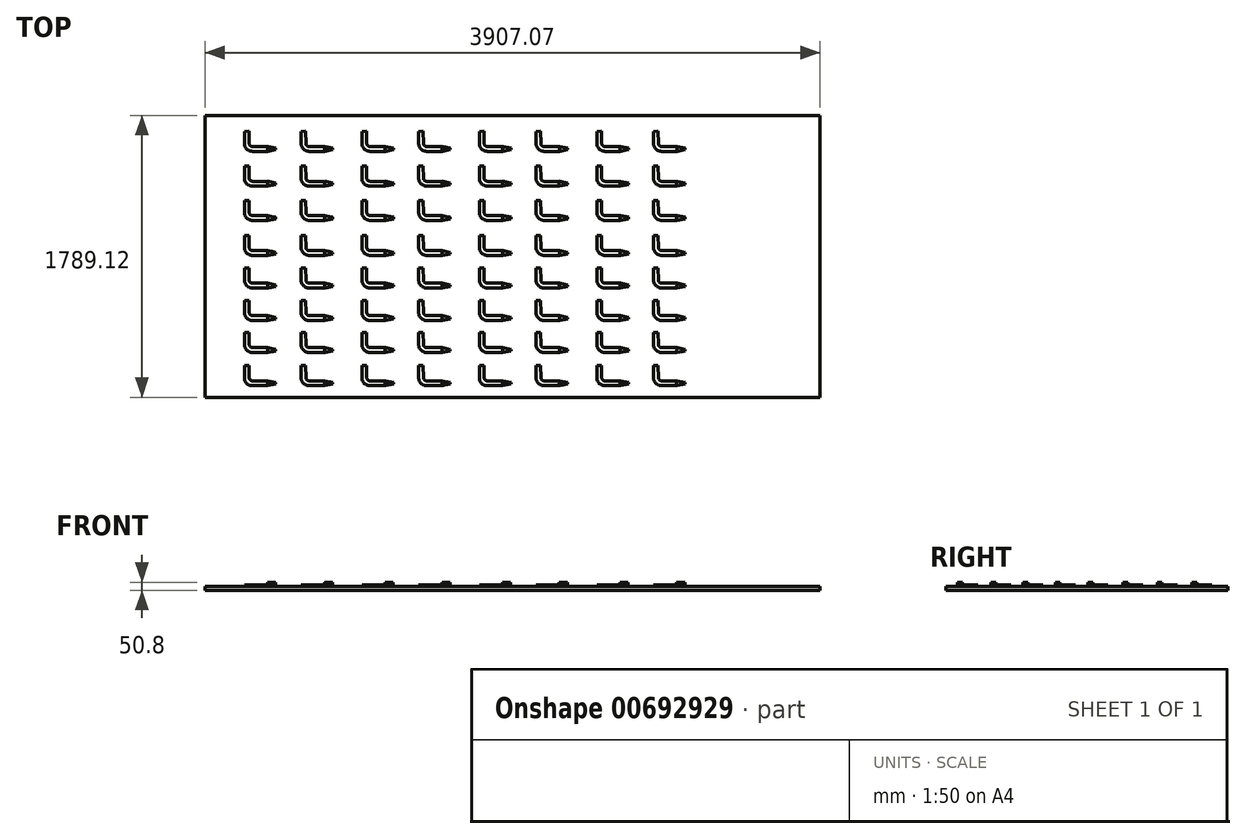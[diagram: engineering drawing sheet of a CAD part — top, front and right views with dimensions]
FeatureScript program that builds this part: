
annotation { "Feature Type Name" : "Feature", "Feature Type Description" : "" }
export const myFeature = defineFeature(function(context is Context, id is Id, definition is map)
    precondition{}
    {
        {
            var Q0;
            Q0=qCreatedBy(makeId("Top.planeOp"),FACE);
            var sketch = newSketch(context, id + "F0", { "sketchPlane" : qUnion([Q0])});
            skLineSegment(sketch, "E0.left", {"start": v(-450.35, 1286.27) * mm, "end": v(-450.35, -502.85) * mm});
            skPoint(sketch, "E0.middle", {"position": v(0, 0) * mm});
            skLineSegment(sketch, "E1", {"start": v(-450.35, 1286.27) * mm, "end": v(3456.72, 1286.27) * mm});
            skLineSegment(sketch, "E2", {"start": v(3456.72, 1286.27) * mm, "end": v(3456.72, -502.85) * mm});
            skLineSegment(sketch, "E3", {"start": v(3456.72, -502.85) * mm, "end": v(-450.35, -502.85) * mm});
            skSolve(sketch);
        }
        {
            var Q0;
            Q0=qSketchRegion(id+"F0",true);
            var Q1;
            Q1=makeQuery(id+"F0.imprint","IMPRINT",FACE,{"disambiguationData":[TD([[makeQuery(id+"F0.imprint","IMPRINT",EDGE,{"derivedFrom":sQuery(id+"F0.wireOp",EDGE,"E0.bottom")}),-1.0]])]});
            extrude(context, id + "F1", {"entities" : qUnion([Q0, Q1]), "oppositeDirection" : true, "depth" : 25.4 * mm, "offsetDistance" : 25.4 * mm});
        }
        {
            var Q0;
            Q0=makeQuery(id+"F1.opExtrude","CAP_FACE",FACE,{"disambiguationData":[OSD([sQuery(id+"F0.wireOp",EDGE,"E0.bottom"),sQuery(id+"F0.wireOp",EDGE,"E0.top"),sQuery(id+"F0.wireOp",EDGE,"E0.left"),sQuery(id+"F0.wireOp",EDGE,"E0.right")])],"isStart":true});
            var sketch = newSketch(context, id + "F2", { "sketchPlane" : qUnion([Q0])});
            skLineSegment(sketch, "E4", {"start": v(-51.41, 16.02) * mm, "end": v(0, 4.87) * mm});
            skLineSegment(sketch, "E5", {"start": v(0, 4.87) * mm, "end": v(0, -4.87) * mm});
            skLineSegment(sketch, "E6", {"start": v(0, -4.87) * mm, "end": v(-51.41, -14.6) * mm});
            skLineSegment(sketch, "E7", {"start": v(-51.41, 16.02) * mm, "end": v(-149.21, 16.02) * mm});
            skLineSegment(sketch, "E8", {"start": v(-149.21, -14.6) * mm, "end": v(-51.41, -14.6) * mm});
            skArc(sketch, "E9", {"start": v(-149.21, 16.02) * mm, "mid": v(-163.12, 21.71) * mm, "end": v(-169.05, 35.52) * mm});
            skArc(sketch, "E10", {"start": v(-149.21, -14.6) * mm, "mid": v(-184.84, 0.05) * mm, "end": v(-199.87, 35.52) * mm});
            skLineSegment(sketch, "E11", {"start": v(-169.05, 35.52) * mm, "end": v(-170.37, 112.54) * mm});
            skLineSegment(sketch, "E12", {"start": v(-170.37, 112.54) * mm, "end": v(-199.87, 112.03) * mm});
            skLineSegment(sketch, "E13", {"start": v(-199.87, 112.03) * mm, "end": v(-199.87, 35.52) * mm});
            skLineSegment(sketch, "E14", {"start": v(-51.41, 221.54) * mm, "end": v(0, 210.39) * mm});
            skLineSegment(sketch, "E15", {"start": v(0, 210.39) * mm, "end": v(0, 200.65) * mm});
            skLineSegment(sketch, "E16", {"start": v(0, 200.65) * mm, "end": v(-51.41, 190.92) * mm});
            skLineSegment(sketch, "E17", {"start": v(-51.41, 221.54) * mm, "end": v(-149.21, 221.54) * mm});
            skLineSegment(sketch, "E18", {"start": v(-149.21, 190.92) * mm, "end": v(-51.41, 190.92) * mm});
            skArc(sketch, "E19", {"start": v(-149.21, 221.54) * mm, "mid": v(-163.12, 227.23) * mm, "end": v(-169.05, 241.04) * mm});
            skArc(sketch, "E20", {"start": v(-149.21, 190.92) * mm, "mid": v(-184.84, 205.56) * mm, "end": v(-199.87, 241.04) * mm});
            skLineSegment(sketch, "E21", {"start": v(-169.05, 241.04) * mm, "end": v(-170.37, 318.06) * mm});
            skLineSegment(sketch, "E22", {"start": v(-170.37, 318.06) * mm, "end": v(-199.87, 317.55) * mm});
            skLineSegment(sketch, "E23", {"start": v(-199.87, 317.55) * mm, "end": v(-199.87, 241.04) * mm});
            skLineSegment(sketch, "E24", {"start": v(-51.41, -187.5) * mm, "end": v(0, -198.65) * mm});
            skLineSegment(sketch, "E25", {"start": v(0, -198.65) * mm, "end": v(0, -208.39) * mm});
            skLineSegment(sketch, "E26", {"start": v(0, -208.39) * mm, "end": v(-51.41, -218.12) * mm});
            skLineSegment(sketch, "E27", {"start": v(-51.41, -187.5) * mm, "end": v(-149.21, -187.5) * mm});
            skLineSegment(sketch, "E28", {"start": v(-149.21, -218.12) * mm, "end": v(-51.41, -218.12) * mm});
            skArc(sketch, "E29", {"start": v(-149.21, -187.5) * mm, "mid": v(-163.12, -181.8) * mm, "end": v(-169.05, -168) * mm});
            skArc(sketch, "E30", {"start": v(-149.21, -218.12) * mm, "mid": v(-184.84, -203.48) * mm, "end": v(-199.87, -168) * mm});
            skLineSegment(sketch, "E31", {"start": v(-169.05, -168) * mm, "end": v(-170.37, -90.98) * mm});
            skLineSegment(sketch, "E32", {"start": v(-170.37, -90.98) * mm, "end": v(-199.87, -91.49) * mm});
            skLineSegment(sketch, "E33", {"start": v(-199.87, -91.49) * mm, "end": v(-199.87, -168) * mm});
            skLineSegment(sketch, "E34", {"start": v(-51.41, -398.32) * mm, "end": v(0, -409.47) * mm});
            skLineSegment(sketch, "E35", {"start": v(0, -409.47) * mm, "end": v(0, -419.2) * mm});
            skLineSegment(sketch, "E36", {"start": v(0, -419.2) * mm, "end": v(-51.41, -428.94) * mm});
            skLineSegment(sketch, "E37", {"start": v(-51.41, -398.32) * mm, "end": v(-149.21, -398.32) * mm});
            skLineSegment(sketch, "E38", {"start": v(-149.21, -428.94) * mm, "end": v(-51.41, -428.94) * mm});
            skArc(sketch, "E39", {"start": v(-149.21, -398.32) * mm, "mid": v(-163.12, -392.63) * mm, "end": v(-169.05, -378.82) * mm});
            skArc(sketch, "E40", {"start": v(-149.21, -428.94) * mm, "mid": v(-184.84, -414.3) * mm, "end": v(-199.87, -378.82) * mm});
            skLineSegment(sketch, "E41", {"start": v(-169.05, -378.82) * mm, "end": v(-170.37, -301.8) * mm});
            skLineSegment(sketch, "E42", {"start": v(-170.37, -301.8) * mm, "end": v(-199.87, -302.3) * mm});
            skLineSegment(sketch, "E43", {"start": v(-199.87, -302.3) * mm, "end": v(-199.87, -378.82) * mm});
            skLineSegment(sketch, "E44", {"start": v(-51.41, 429.24) * mm, "end": v(0, 418.08) * mm});
            skLineSegment(sketch, "E45", {"start": v(0, 418.08) * mm, "end": v(0, 408.35) * mm});
            skLineSegment(sketch, "E46", {"start": v(0, 408.35) * mm, "end": v(-51.41, 398.61) * mm});
            skLineSegment(sketch, "E47", {"start": v(-51.41, 429.24) * mm, "end": v(-149.21, 429.24) * mm});
            skLineSegment(sketch, "E48", {"start": v(-149.21, 398.61) * mm, "end": v(-51.41, 398.61) * mm});
            skArc(sketch, "E49", {"start": v(-149.21, 429.24) * mm, "mid": v(-163.12, 434.93) * mm, "end": v(-169.05, 448.73) * mm});
            skArc(sketch, "E50", {"start": v(-149.21, 398.61) * mm, "mid": v(-184.84, 413.26) * mm, "end": v(-199.87, 448.73) * mm});
            skLineSegment(sketch, "E51", {"start": v(-169.05, 448.73) * mm, "end": v(-170.37, 525.76) * mm});
            skLineSegment(sketch, "E52", {"start": v(-170.37, 525.76) * mm, "end": v(-199.87, 525.25) * mm});
            skLineSegment(sketch, "E53", {"start": v(-199.87, 525.25) * mm, "end": v(-199.87, 448.73) * mm});
            skLineSegment(sketch, "E54", {"start": v(-51.41, 651.7) * mm, "end": v(0, 640.54) * mm});
            skLineSegment(sketch, "E55", {"start": v(0, 640.54) * mm, "end": v(0, 630.8) * mm});
            skLineSegment(sketch, "E56", {"start": v(0, 630.8) * mm, "end": v(-51.41, 621.07) * mm});
            skLineSegment(sketch, "E57", {"start": v(-51.41, 651.7) * mm, "end": v(-149.21, 651.7) * mm});
            skLineSegment(sketch, "E58", {"start": v(-149.21, 621.07) * mm, "end": v(-51.41, 621.07) * mm});
            skArc(sketch, "E59", {"start": v(-149.21, 651.7) * mm, "mid": v(-163.12, 657.39) * mm, "end": v(-169.05, 671.2) * mm});
            skArc(sketch, "E60", {"start": v(-149.21, 621.07) * mm, "mid": v(-184.84, 635.72) * mm, "end": v(-199.87, 671.2) * mm});
            skLineSegment(sketch, "E61", {"start": v(-169.05, 671.2) * mm, "end": v(-170.37, 748.22) * mm});
            skLineSegment(sketch, "E62", {"start": v(-170.37, 748.22) * mm, "end": v(-199.87, 747.71) * mm});
            skLineSegment(sketch, "E63", {"start": v(-199.87, 747.71) * mm, "end": v(-199.87, 671.2) * mm});
            skLineSegment(sketch, "E64", {"start": v(-51.41, 869.02) * mm, "end": v(0, 857.87) * mm});
            skLineSegment(sketch, "E65", {"start": v(0, 857.87) * mm, "end": v(0, 848.13) * mm});
            skLineSegment(sketch, "E66", {"start": v(0, 848.13) * mm, "end": v(-51.41, 838.4) * mm});
            skLineSegment(sketch, "E67", {"start": v(-51.41, 869.02) * mm, "end": v(-149.21, 869.02) * mm});
            skLineSegment(sketch, "E68", {"start": v(-149.21, 838.4) * mm, "end": v(-51.41, 838.4) * mm});
            skArc(sketch, "E69", {"start": v(-149.21, 869.02) * mm, "mid": v(-163.12, 874.71) * mm, "end": v(-169.05, 888.52) * mm});
            skArc(sketch, "E70", {"start": v(-149.21, 838.4) * mm, "mid": v(-184.84, 853.05) * mm, "end": v(-199.87, 888.52) * mm});
            skLineSegment(sketch, "E71", {"start": v(-169.05, 888.52) * mm, "end": v(-170.37, 965.54) * mm});
            skLineSegment(sketch, "E72", {"start": v(-170.37, 965.54) * mm, "end": v(-199.87, 965.04) * mm});
            skLineSegment(sketch, "E73", {"start": v(-199.87, 965.04) * mm, "end": v(-199.87, 888.52) * mm});
            skLineSegment(sketch, "E74", {"start": v(-51.41, 1090.15) * mm, "end": v(0, 1079) * mm});
            skLineSegment(sketch, "E75", {"start": v(0, 1079) * mm, "end": v(0, 1069.26) * mm});
            skLineSegment(sketch, "E76", {"start": v(0, 1069.26) * mm, "end": v(-51.41, 1059.52) * mm});
            skLineSegment(sketch, "E77", {"start": v(-51.41, 1090.15) * mm, "end": v(-149.21, 1090.15) * mm});
            skLineSegment(sketch, "E78", {"start": v(-149.21, 1059.52) * mm, "end": v(-51.41, 1059.52) * mm});
            skArc(sketch, "E79", {"start": v(-149.21, 1090.15) * mm, "mid": v(-163.12, 1095.84) * mm, "end": v(-169.05, 1109.64) * mm});
            skArc(sketch, "E80", {"start": v(-149.21, 1059.52) * mm, "mid": v(-184.84, 1074.17) * mm, "end": v(-199.87, 1109.64) * mm});
            skLineSegment(sketch, "E81", {"start": v(-169.05, 1109.64) * mm, "end": v(-170.37, 1186.67) * mm});
            skLineSegment(sketch, "E82", {"start": v(-170.37, 1186.67) * mm, "end": v(-199.87, 1186.16) * mm});
            skLineSegment(sketch, "E83", {"start": v(-199.87, 1186.16) * mm, "end": v(-199.87, 1109.64) * mm});
            skLineSegment(sketch, "E84", {"start": v(308.62, 16.02) * mm, "end": v(360.03, 4.87) * mm});
            skLineSegment(sketch, "E85", {"start": v(360.03, 4.87) * mm, "end": v(360.03, -4.87) * mm});
            skLineSegment(sketch, "E86", {"start": v(360.03, -4.87) * mm, "end": v(308.62, -14.6) * mm});
            skLineSegment(sketch, "E87", {"start": v(308.62, 16.02) * mm, "end": v(210.82, 16.02) * mm});
            skLineSegment(sketch, "E88", {"start": v(210.82, -14.6) * mm, "end": v(308.62, -14.6) * mm});
            skArc(sketch, "E89", {"start": v(210.82, 16.02) * mm, "mid": v(196.91, 21.71) * mm, "end": v(190.99, 35.52) * mm});
            skArc(sketch, "E90", {"start": v(210.82, -14.6) * mm, "mid": v(175.19, 0.05) * mm, "end": v(160.16, 35.52) * mm});
            skLineSegment(sketch, "E91", {"start": v(190.99, 35.52) * mm, "end": v(189.66, 112.54) * mm});
            skLineSegment(sketch, "E92", {"start": v(189.66, 112.54) * mm, "end": v(160.16, 112.03) * mm});
            skLineSegment(sketch, "E93", {"start": v(160.16, 112.03) * mm, "end": v(160.16, 35.52) * mm});
            skLineSegment(sketch, "E94", {"start": v(308.62, 221.54) * mm, "end": v(360.03, 210.39) * mm});
            skLineSegment(sketch, "E95", {"start": v(360.03, 210.39) * mm, "end": v(360.03, 200.65) * mm});
            skLineSegment(sketch, "E96", {"start": v(360.03, 200.65) * mm, "end": v(308.62, 190.92) * mm});
            skLineSegment(sketch, "E97", {"start": v(308.62, 221.54) * mm, "end": v(210.82, 221.54) * mm});
            skLineSegment(sketch, "E98", {"start": v(210.82, 190.92) * mm, "end": v(308.62, 190.92) * mm});
            skArc(sketch, "E99", {"start": v(210.82, 221.54) * mm, "mid": v(196.91, 227.23) * mm, "end": v(190.99, 241.04) * mm});
            skArc(sketch, "E100", {"start": v(210.82, 190.92) * mm, "mid": v(175.19, 205.56) * mm, "end": v(160.16, 241.04) * mm});
            skLineSegment(sketch, "E101", {"start": v(190.99, 241.04) * mm, "end": v(189.66, 318.06) * mm});
            skLineSegment(sketch, "E102", {"start": v(189.66, 318.06) * mm, "end": v(160.16, 317.55) * mm});
            skLineSegment(sketch, "E103", {"start": v(160.16, 317.55) * mm, "end": v(160.16, 241.04) * mm});
            skLineSegment(sketch, "E104", {"start": v(308.62, -187.5) * mm, "end": v(360.03, -198.65) * mm});
            skLineSegment(sketch, "E105", {"start": v(360.03, -198.65) * mm, "end": v(360.03, -208.39) * mm});
            skLineSegment(sketch, "E106", {"start": v(360.03, -208.39) * mm, "end": v(308.62, -218.12) * mm});
            skLineSegment(sketch, "E107", {"start": v(308.62, -187.5) * mm, "end": v(210.82, -187.5) * mm});
            skLineSegment(sketch, "E108", {"start": v(210.82, -218.12) * mm, "end": v(308.62, -218.12) * mm});
            skArc(sketch, "E109", {"start": v(210.82, -187.5) * mm, "mid": v(196.91, -181.8) * mm, "end": v(190.99, -168) * mm});
            skArc(sketch, "E110", {"start": v(210.82, -218.12) * mm, "mid": v(175.19, -203.48) * mm, "end": v(160.16, -168) * mm});
            skLineSegment(sketch, "E111", {"start": v(190.99, -168) * mm, "end": v(189.66, -90.98) * mm});
            skLineSegment(sketch, "E112", {"start": v(189.66, -90.98) * mm, "end": v(160.16, -91.49) * mm});
            skLineSegment(sketch, "E113", {"start": v(160.16, -91.49) * mm, "end": v(160.16, -168) * mm});
            skLineSegment(sketch, "E114", {"start": v(308.62, -398.32) * mm, "end": v(360.03, -409.47) * mm});
            skLineSegment(sketch, "E115", {"start": v(360.03, -409.47) * mm, "end": v(360.03, -419.2) * mm});
            skLineSegment(sketch, "E116", {"start": v(360.03, -419.2) * mm, "end": v(308.62, -428.94) * mm});
            skLineSegment(sketch, "E117", {"start": v(308.62, -398.32) * mm, "end": v(210.82, -398.32) * mm});
            skLineSegment(sketch, "E118", {"start": v(210.82, -428.94) * mm, "end": v(308.62, -428.94) * mm});
            skArc(sketch, "E119", {"start": v(210.82, -398.32) * mm, "mid": v(196.91, -392.63) * mm, "end": v(190.99, -378.82) * mm});
            skArc(sketch, "E120", {"start": v(210.82, -428.94) * mm, "mid": v(175.19, -414.3) * mm, "end": v(160.16, -378.82) * mm});
            skLineSegment(sketch, "E121", {"start": v(190.99, -378.82) * mm, "end": v(189.66, -301.8) * mm});
            skLineSegment(sketch, "E122", {"start": v(189.66, -301.8) * mm, "end": v(160.16, -302.3) * mm});
            skLineSegment(sketch, "E123", {"start": v(160.16, -302.3) * mm, "end": v(160.16, -378.82) * mm});
            skLineSegment(sketch, "E124", {"start": v(308.62, 429.24) * mm, "end": v(360.03, 418.08) * mm});
            skLineSegment(sketch, "E125", {"start": v(360.03, 418.08) * mm, "end": v(360.03, 408.35) * mm});
            skLineSegment(sketch, "E126", {"start": v(360.03, 408.35) * mm, "end": v(308.62, 398.61) * mm});
            skLineSegment(sketch, "E127", {"start": v(308.62, 429.24) * mm, "end": v(210.82, 429.24) * mm});
            skLineSegment(sketch, "E128", {"start": v(210.82, 398.61) * mm, "end": v(308.62, 398.61) * mm});
            skArc(sketch, "E129", {"start": v(210.82, 429.24) * mm, "mid": v(196.91, 434.93) * mm, "end": v(190.99, 448.73) * mm});
            skArc(sketch, "E130", {"start": v(210.82, 398.61) * mm, "mid": v(175.19, 413.26) * mm, "end": v(160.16, 448.73) * mm});
            skLineSegment(sketch, "E131", {"start": v(190.99, 448.73) * mm, "end": v(189.66, 525.76) * mm});
            skLineSegment(sketch, "E132", {"start": v(189.66, 525.76) * mm, "end": v(160.16, 525.25) * mm});
            skLineSegment(sketch, "E133", {"start": v(160.16, 525.25) * mm, "end": v(160.16, 448.73) * mm});
            skLineSegment(sketch, "E134", {"start": v(308.62, 651.7) * mm, "end": v(360.03, 640.54) * mm});
            skLineSegment(sketch, "E135", {"start": v(360.03, 640.54) * mm, "end": v(360.03, 630.8) * mm});
            skLineSegment(sketch, "E136", {"start": v(360.03, 630.8) * mm, "end": v(308.62, 621.07) * mm});
            skLineSegment(sketch, "E137", {"start": v(308.62, 651.7) * mm, "end": v(210.82, 651.7) * mm});
            skLineSegment(sketch, "E138", {"start": v(210.82, 621.07) * mm, "end": v(308.62, 621.07) * mm});
            skArc(sketch, "E139", {"start": v(210.82, 651.7) * mm, "mid": v(196.91, 657.39) * mm, "end": v(190.99, 671.2) * mm});
            skArc(sketch, "E140", {"start": v(210.82, 621.07) * mm, "mid": v(175.19, 635.72) * mm, "end": v(160.16, 671.2) * mm});
            skLineSegment(sketch, "E141", {"start": v(190.99, 671.2) * mm, "end": v(189.66, 748.22) * mm});
            skLineSegment(sketch, "E142", {"start": v(189.66, 748.22) * mm, "end": v(160.16, 747.71) * mm});
            skLineSegment(sketch, "E143", {"start": v(160.16, 747.71) * mm, "end": v(160.16, 671.2) * mm});
            skLineSegment(sketch, "E144", {"start": v(308.62, 869.02) * mm, "end": v(360.03, 857.87) * mm});
            skLineSegment(sketch, "E145", {"start": v(360.03, 857.87) * mm, "end": v(360.03, 848.13) * mm});
            skLineSegment(sketch, "E146", {"start": v(360.03, 848.13) * mm, "end": v(308.62, 838.4) * mm});
            skLineSegment(sketch, "E147", {"start": v(308.62, 869.02) * mm, "end": v(210.82, 869.02) * mm});
            skLineSegment(sketch, "E148", {"start": v(210.82, 838.4) * mm, "end": v(308.62, 838.4) * mm});
            skArc(sketch, "E149", {"start": v(210.82, 869.02) * mm, "mid": v(196.91, 874.71) * mm, "end": v(190.99, 888.52) * mm});
            skArc(sketch, "E150", {"start": v(210.82, 838.4) * mm, "mid": v(175.19, 853.05) * mm, "end": v(160.16, 888.52) * mm});
            skLineSegment(sketch, "E151", {"start": v(190.99, 888.52) * mm, "end": v(189.66, 965.54) * mm});
            skLineSegment(sketch, "E152", {"start": v(189.66, 965.54) * mm, "end": v(160.16, 965.04) * mm});
            skLineSegment(sketch, "E153", {"start": v(160.16, 965.04) * mm, "end": v(160.16, 888.52) * mm});
            skLineSegment(sketch, "E154", {"start": v(308.62, 1090.15) * mm, "end": v(360.03, 1079) * mm});
            skLineSegment(sketch, "E155", {"start": v(360.03, 1079) * mm, "end": v(360.03, 1069.26) * mm});
            skLineSegment(sketch, "E156", {"start": v(360.03, 1069.26) * mm, "end": v(308.62, 1059.52) * mm});
            skLineSegment(sketch, "E157", {"start": v(308.62, 1090.15) * mm, "end": v(210.82, 1090.15) * mm});
            skLineSegment(sketch, "E158", {"start": v(210.82, 1059.52) * mm, "end": v(308.62, 1059.52) * mm});
            skArc(sketch, "E159", {"start": v(210.82, 1090.15) * mm, "mid": v(196.91, 1095.84) * mm, "end": v(190.99, 1109.64) * mm});
            skArc(sketch, "E160", {"start": v(210.82, 1059.52) * mm, "mid": v(175.19, 1074.17) * mm, "end": v(160.16, 1109.64) * mm});
            skLineSegment(sketch, "E161", {"start": v(190.99, 1109.64) * mm, "end": v(189.66, 1186.67) * mm});
            skLineSegment(sketch, "E162", {"start": v(189.66, 1186.67) * mm, "end": v(160.16, 1186.16) * mm});
            skLineSegment(sketch, "E163", {"start": v(160.16, 1186.16) * mm, "end": v(160.16, 1109.64) * mm});
            skLineSegment(sketch, "E164", {"start": v(695.34, 16.02) * mm, "end": v(746.75, 4.87) * mm});
            skLineSegment(sketch, "E165", {"start": v(746.75, 4.87) * mm, "end": v(746.75, -4.87) * mm});
            skLineSegment(sketch, "E166", {"start": v(746.75, -4.87) * mm, "end": v(695.34, -14.6) * mm});
            skLineSegment(sketch, "E167", {"start": v(695.34, 16.02) * mm, "end": v(597.54, 16.02) * mm});
            skLineSegment(sketch, "E168", {"start": v(597.54, -14.6) * mm, "end": v(695.34, -14.6) * mm});
            skArc(sketch, "E169", {"start": v(597.54, 16.02) * mm, "mid": v(583.63, 21.71) * mm, "end": v(577.7, 35.52) * mm});
            skArc(sketch, "E170", {"start": v(597.54, -14.6) * mm, "mid": v(561.9, 0.05) * mm, "end": v(546.88, 35.52) * mm});
            skLineSegment(sketch, "E171", {"start": v(577.7, 35.52) * mm, "end": v(576.38, 112.54) * mm});
            skLineSegment(sketch, "E172", {"start": v(576.38, 112.54) * mm, "end": v(546.88, 112.03) * mm});
            skLineSegment(sketch, "E173", {"start": v(546.88, 112.03) * mm, "end": v(546.88, 35.52) * mm});
            skLineSegment(sketch, "E174", {"start": v(695.34, 221.54) * mm, "end": v(746.75, 210.39) * mm});
            skLineSegment(sketch, "E175", {"start": v(746.75, 210.39) * mm, "end": v(746.75, 200.65) * mm});
            skLineSegment(sketch, "E176", {"start": v(746.75, 200.65) * mm, "end": v(695.34, 190.92) * mm});
            skLineSegment(sketch, "E177", {"start": v(695.34, 221.54) * mm, "end": v(597.54, 221.54) * mm});
            skLineSegment(sketch, "E178", {"start": v(597.54, 190.92) * mm, "end": v(695.34, 190.92) * mm});
            skArc(sketch, "E179", {"start": v(597.54, 221.54) * mm, "mid": v(583.63, 227.23) * mm, "end": v(577.7, 241.04) * mm});
            skArc(sketch, "E180", {"start": v(597.54, 190.92) * mm, "mid": v(561.9, 205.56) * mm, "end": v(546.88, 241.04) * mm});
            skLineSegment(sketch, "E181", {"start": v(577.7, 241.04) * mm, "end": v(576.38, 318.06) * mm});
            skLineSegment(sketch, "E182", {"start": v(576.38, 318.06) * mm, "end": v(546.88, 317.55) * mm});
            skLineSegment(sketch, "E183", {"start": v(546.88, 317.55) * mm, "end": v(546.88, 241.04) * mm});
            skLineSegment(sketch, "E184", {"start": v(695.34, -187.5) * mm, "end": v(746.75, -198.65) * mm});
            skLineSegment(sketch, "E185", {"start": v(746.75, -198.65) * mm, "end": v(746.75, -208.39) * mm});
            skLineSegment(sketch, "E186", {"start": v(746.75, -208.39) * mm, "end": v(695.34, -218.12) * mm});
            skLineSegment(sketch, "E187", {"start": v(695.34, -187.5) * mm, "end": v(597.54, -187.5) * mm});
            skLineSegment(sketch, "E188", {"start": v(597.54, -218.12) * mm, "end": v(695.34, -218.12) * mm});
            skArc(sketch, "E189", {"start": v(597.54, -187.5) * mm, "mid": v(583.63, -181.8) * mm, "end": v(577.7, -168) * mm});
            skArc(sketch, "E190", {"start": v(597.54, -218.12) * mm, "mid": v(561.9, -203.48) * mm, "end": v(546.88, -168) * mm});
            skLineSegment(sketch, "E191", {"start": v(577.7, -168) * mm, "end": v(576.38, -90.98) * mm});
            skLineSegment(sketch, "E192", {"start": v(576.38, -90.98) * mm, "end": v(546.88, -91.49) * mm});
            skLineSegment(sketch, "E193", {"start": v(546.88, -91.49) * mm, "end": v(546.88, -168) * mm});
            skLineSegment(sketch, "E194", {"start": v(695.34, -398.32) * mm, "end": v(746.75, -409.47) * mm});
            skLineSegment(sketch, "E195", {"start": v(746.75, -409.47) * mm, "end": v(746.75, -419.2) * mm});
            skLineSegment(sketch, "E196", {"start": v(746.75, -419.2) * mm, "end": v(695.34, -428.94) * mm});
            skLineSegment(sketch, "E197", {"start": v(695.34, -398.32) * mm, "end": v(597.54, -398.32) * mm});
            skLineSegment(sketch, "E198", {"start": v(597.54, -428.94) * mm, "end": v(695.34, -428.94) * mm});
            skArc(sketch, "E199", {"start": v(597.54, -398.32) * mm, "mid": v(583.63, -392.63) * mm, "end": v(577.7, -378.82) * mm});
            skArc(sketch, "E200", {"start": v(597.54, -428.94) * mm, "mid": v(561.9, -414.3) * mm, "end": v(546.88, -378.82) * mm});
            skLineSegment(sketch, "E201", {"start": v(577.7, -378.82) * mm, "end": v(576.38, -301.8) * mm});
            skLineSegment(sketch, "E202", {"start": v(576.38, -301.8) * mm, "end": v(546.88, -302.3) * mm});
            skLineSegment(sketch, "E203", {"start": v(546.88, -302.3) * mm, "end": v(546.88, -378.82) * mm});
            skLineSegment(sketch, "E204", {"start": v(695.34, 429.24) * mm, "end": v(746.75, 418.08) * mm});
            skLineSegment(sketch, "E205", {"start": v(746.75, 418.08) * mm, "end": v(746.75, 408.35) * mm});
            skLineSegment(sketch, "E206", {"start": v(746.75, 408.35) * mm, "end": v(695.34, 398.61) * mm});
            skLineSegment(sketch, "E207", {"start": v(695.34, 429.24) * mm, "end": v(597.54, 429.24) * mm});
            skLineSegment(sketch, "E208", {"start": v(597.54, 398.61) * mm, "end": v(695.34, 398.61) * mm});
            skArc(sketch, "E209", {"start": v(597.54, 429.24) * mm, "mid": v(583.63, 434.93) * mm, "end": v(577.7, 448.73) * mm});
            skArc(sketch, "E210", {"start": v(597.54, 398.61) * mm, "mid": v(561.9, 413.26) * mm, "end": v(546.88, 448.73) * mm});
            skLineSegment(sketch, "E211", {"start": v(577.7, 448.73) * mm, "end": v(576.38, 525.76) * mm});
            skLineSegment(sketch, "E212", {"start": v(576.38, 525.76) * mm, "end": v(546.88, 525.25) * mm});
            skLineSegment(sketch, "E213", {"start": v(546.88, 525.25) * mm, "end": v(546.88, 448.73) * mm});
            skLineSegment(sketch, "E214", {"start": v(695.34, 651.7) * mm, "end": v(746.75, 640.54) * mm});
            skLineSegment(sketch, "E215", {"start": v(746.75, 640.54) * mm, "end": v(746.75, 630.8) * mm});
            skLineSegment(sketch, "E216", {"start": v(746.75, 630.8) * mm, "end": v(695.34, 621.07) * mm});
            skLineSegment(sketch, "E217", {"start": v(695.34, 651.7) * mm, "end": v(597.54, 651.7) * mm});
            skLineSegment(sketch, "E218", {"start": v(597.54, 621.07) * mm, "end": v(695.34, 621.07) * mm});
            skArc(sketch, "E219", {"start": v(597.54, 651.7) * mm, "mid": v(583.63, 657.39) * mm, "end": v(577.7, 671.2) * mm});
            skArc(sketch, "E220", {"start": v(597.54, 621.07) * mm, "mid": v(561.9, 635.72) * mm, "end": v(546.88, 671.2) * mm});
            skLineSegment(sketch, "E221", {"start": v(577.7, 671.2) * mm, "end": v(576.38, 748.22) * mm});
            skLineSegment(sketch, "E222", {"start": v(576.38, 748.22) * mm, "end": v(546.88, 747.71) * mm});
            skLineSegment(sketch, "E223", {"start": v(546.88, 747.71) * mm, "end": v(546.88, 671.2) * mm});
            skLineSegment(sketch, "E224", {"start": v(695.34, 869.02) * mm, "end": v(746.75, 857.87) * mm});
            skLineSegment(sketch, "E225", {"start": v(746.75, 857.87) * mm, "end": v(746.75, 848.13) * mm});
            skLineSegment(sketch, "E226", {"start": v(746.75, 848.13) * mm, "end": v(695.34, 838.4) * mm});
            skLineSegment(sketch, "E227", {"start": v(695.34, 869.02) * mm, "end": v(597.54, 869.02) * mm});
            skLineSegment(sketch, "E228", {"start": v(597.54, 838.4) * mm, "end": v(695.34, 838.4) * mm});
            skArc(sketch, "E229", {"start": v(597.54, 869.02) * mm, "mid": v(583.63, 874.71) * mm, "end": v(577.7, 888.52) * mm});
            skArc(sketch, "E230", {"start": v(597.54, 838.4) * mm, "mid": v(561.9, 853.05) * mm, "end": v(546.88, 888.52) * mm});
            skLineSegment(sketch, "E231", {"start": v(577.7, 888.52) * mm, "end": v(576.38, 965.54) * mm});
            skLineSegment(sketch, "E232", {"start": v(576.38, 965.54) * mm, "end": v(546.88, 965.04) * mm});
            skLineSegment(sketch, "E233", {"start": v(546.88, 965.04) * mm, "end": v(546.88, 888.52) * mm});
            skLineSegment(sketch, "E234", {"start": v(695.34, 1090.15) * mm, "end": v(746.75, 1079) * mm});
            skLineSegment(sketch, "E235", {"start": v(746.75, 1079) * mm, "end": v(746.75, 1069.26) * mm});
            skLineSegment(sketch, "E236", {"start": v(746.75, 1069.26) * mm, "end": v(695.34, 1059.52) * mm});
            skLineSegment(sketch, "E237", {"start": v(695.34, 1090.15) * mm, "end": v(597.54, 1090.15) * mm});
            skLineSegment(sketch, "E238", {"start": v(597.54, 1059.52) * mm, "end": v(695.34, 1059.52) * mm});
            skArc(sketch, "E239", {"start": v(597.54, 1090.15) * mm, "mid": v(583.63, 1095.84) * mm, "end": v(577.7, 1109.64) * mm});
            skArc(sketch, "E240", {"start": v(597.54, 1059.52) * mm, "mid": v(561.9, 1074.17) * mm, "end": v(546.88, 1109.64) * mm});
            skLineSegment(sketch, "E241", {"start": v(577.7, 1109.64) * mm, "end": v(576.38, 1186.67) * mm});
            skLineSegment(sketch, "E242", {"start": v(576.38, 1186.67) * mm, "end": v(546.88, 1186.16) * mm});
            skLineSegment(sketch, "E243", {"start": v(546.88, 1186.16) * mm, "end": v(546.88, 1109.64) * mm});
            skLineSegment(sketch, "E244", {"start": v(1055.37, 16.02) * mm, "end": v(1106.78, 4.87) * mm});
            skLineSegment(sketch, "E245", {"start": v(1106.78, 4.87) * mm, "end": v(1106.78, -4.87) * mm});
            skLineSegment(sketch, "E246", {"start": v(1106.78, -4.87) * mm, "end": v(1055.37, -14.6) * mm});
            skLineSegment(sketch, "E247", {"start": v(1055.37, 16.02) * mm, "end": v(957.57, 16.02) * mm});
            skLineSegment(sketch, "E248", {"start": v(957.57, -14.6) * mm, "end": v(1055.37, -14.6) * mm});
            skArc(sketch, "E249", {"start": v(957.57, 16.02) * mm, "mid": v(943.67, 21.71) * mm, "end": v(937.74, 35.52) * mm});
            skArc(sketch, "E250", {"start": v(957.57, -14.6) * mm, "mid": v(921.94, 0.05) * mm, "end": v(906.9, 35.52) * mm});
            skLineSegment(sketch, "E251", {"start": v(937.74, 35.52) * mm, "end": v(936.41, 112.54) * mm});
            skLineSegment(sketch, "E252", {"start": v(936.41, 112.54) * mm, "end": v(906.9, 112.03) * mm});
            skLineSegment(sketch, "E253", {"start": v(906.9, 112.03) * mm, "end": v(906.9, 35.52) * mm});
            skLineSegment(sketch, "E254", {"start": v(1055.37, 221.54) * mm, "end": v(1106.78, 210.39) * mm});
            skLineSegment(sketch, "E255", {"start": v(1106.78, 210.39) * mm, "end": v(1106.78, 200.65) * mm});
            skLineSegment(sketch, "E256", {"start": v(1106.78, 200.65) * mm, "end": v(1055.37, 190.92) * mm});
            skLineSegment(sketch, "E257", {"start": v(1055.37, 221.54) * mm, "end": v(957.57, 221.54) * mm});
            skLineSegment(sketch, "E258", {"start": v(957.57, 190.92) * mm, "end": v(1055.37, 190.92) * mm});
            skArc(sketch, "E259", {"start": v(957.57, 221.54) * mm, "mid": v(943.67, 227.23) * mm, "end": v(937.74, 241.04) * mm});
            skArc(sketch, "E260", {"start": v(957.57, 190.92) * mm, "mid": v(921.94, 205.56) * mm, "end": v(906.9, 241.04) * mm});
            skLineSegment(sketch, "E261", {"start": v(937.74, 241.04) * mm, "end": v(936.41, 318.06) * mm});
            skLineSegment(sketch, "E262", {"start": v(936.41, 318.06) * mm, "end": v(906.9, 317.55) * mm});
            skLineSegment(sketch, "E263", {"start": v(906.9, 317.55) * mm, "end": v(906.9, 241.04) * mm});
            skLineSegment(sketch, "E264", {"start": v(1055.37, -187.5) * mm, "end": v(1106.78, -198.65) * mm});
            skLineSegment(sketch, "E265", {"start": v(1106.78, -198.65) * mm, "end": v(1106.78, -208.39) * mm});
            skLineSegment(sketch, "E266", {"start": v(1106.78, -208.39) * mm, "end": v(1055.37, -218.12) * mm});
            skLineSegment(sketch, "E267", {"start": v(1055.37, -187.5) * mm, "end": v(957.57, -187.5) * mm});
            skLineSegment(sketch, "E268", {"start": v(957.57, -218.12) * mm, "end": v(1055.37, -218.12) * mm});
            skArc(sketch, "E269", {"start": v(957.57, -187.5) * mm, "mid": v(943.67, -181.8) * mm, "end": v(937.74, -168) * mm});
            skArc(sketch, "E270", {"start": v(957.57, -218.12) * mm, "mid": v(921.94, -203.48) * mm, "end": v(906.9, -168) * mm});
            skLineSegment(sketch, "E271", {"start": v(937.74, -168) * mm, "end": v(936.41, -90.98) * mm});
            skLineSegment(sketch, "E272", {"start": v(936.41, -90.98) * mm, "end": v(906.9, -91.49) * mm});
            skLineSegment(sketch, "E273", {"start": v(906.9, -91.49) * mm, "end": v(906.9, -168) * mm});
            skLineSegment(sketch, "E274", {"start": v(1055.37, -398.32) * mm, "end": v(1106.78, -409.47) * mm});
            skLineSegment(sketch, "E275", {"start": v(1106.78, -409.47) * mm, "end": v(1106.78, -419.2) * mm});
            skLineSegment(sketch, "E276", {"start": v(1106.78, -419.2) * mm, "end": v(1055.37, -428.94) * mm});
            skLineSegment(sketch, "E277", {"start": v(1055.37, -398.32) * mm, "end": v(957.57, -398.32) * mm});
            skLineSegment(sketch, "E278", {"start": v(957.57, -428.94) * mm, "end": v(1055.37, -428.94) * mm});
            skArc(sketch, "E279", {"start": v(957.57, -398.32) * mm, "mid": v(943.67, -392.63) * mm, "end": v(937.74, -378.82) * mm});
            skArc(sketch, "E280", {"start": v(957.57, -428.94) * mm, "mid": v(921.94, -414.3) * mm, "end": v(906.9, -378.82) * mm});
            skLineSegment(sketch, "E281", {"start": v(937.74, -378.82) * mm, "end": v(936.41, -301.8) * mm});
            skLineSegment(sketch, "E282", {"start": v(936.41, -301.8) * mm, "end": v(906.9, -302.3) * mm});
            skLineSegment(sketch, "E283", {"start": v(906.9, -302.3) * mm, "end": v(906.9, -378.82) * mm});
            skLineSegment(sketch, "E284", {"start": v(1055.37, 429.24) * mm, "end": v(1106.78, 418.08) * mm});
            skLineSegment(sketch, "E285", {"start": v(1106.78, 418.08) * mm, "end": v(1106.78, 408.35) * mm});
            skLineSegment(sketch, "E286", {"start": v(1106.78, 408.35) * mm, "end": v(1055.37, 398.61) * mm});
            skLineSegment(sketch, "E287", {"start": v(1055.37, 429.24) * mm, "end": v(957.57, 429.24) * mm});
            skLineSegment(sketch, "E288", {"start": v(957.57, 398.61) * mm, "end": v(1055.37, 398.61) * mm});
            skArc(sketch, "E289", {"start": v(957.57, 429.24) * mm, "mid": v(943.67, 434.93) * mm, "end": v(937.74, 448.73) * mm});
            skArc(sketch, "E290", {"start": v(957.57, 398.61) * mm, "mid": v(921.94, 413.26) * mm, "end": v(906.9, 448.73) * mm});
            skLineSegment(sketch, "E291", {"start": v(937.74, 448.73) * mm, "end": v(936.41, 525.76) * mm});
            skLineSegment(sketch, "E292", {"start": v(936.41, 525.76) * mm, "end": v(906.9, 525.25) * mm});
            skLineSegment(sketch, "E293", {"start": v(906.9, 525.25) * mm, "end": v(906.9, 448.73) * mm});
            skLineSegment(sketch, "E294", {"start": v(1055.37, 651.7) * mm, "end": v(1106.78, 640.54) * mm});
            skLineSegment(sketch, "E295", {"start": v(1106.78, 640.54) * mm, "end": v(1106.78, 630.8) * mm});
            skLineSegment(sketch, "E296", {"start": v(1106.78, 630.8) * mm, "end": v(1055.37, 621.07) * mm});
            skLineSegment(sketch, "E297", {"start": v(1055.37, 651.7) * mm, "end": v(957.57, 651.7) * mm});
            skLineSegment(sketch, "E298", {"start": v(957.57, 621.07) * mm, "end": v(1055.37, 621.07) * mm});
            skArc(sketch, "E299", {"start": v(957.57, 651.7) * mm, "mid": v(943.67, 657.39) * mm, "end": v(937.74, 671.2) * mm});
            skArc(sketch, "E300", {"start": v(957.57, 621.07) * mm, "mid": v(921.94, 635.72) * mm, "end": v(906.9, 671.2) * mm});
            skLineSegment(sketch, "E301", {"start": v(937.74, 671.2) * mm, "end": v(936.41, 748.22) * mm});
            skLineSegment(sketch, "E302", {"start": v(936.41, 748.22) * mm, "end": v(906.9, 747.71) * mm});
            skLineSegment(sketch, "E303", {"start": v(906.9, 747.71) * mm, "end": v(906.9, 671.2) * mm});
            skLineSegment(sketch, "E304", {"start": v(1055.37, 869.02) * mm, "end": v(1106.78, 857.87) * mm});
            skLineSegment(sketch, "E305", {"start": v(1106.78, 857.87) * mm, "end": v(1106.78, 848.13) * mm});
            skLineSegment(sketch, "E306", {"start": v(1106.78, 848.13) * mm, "end": v(1055.37, 838.4) * mm});
            skLineSegment(sketch, "E307", {"start": v(1055.37, 869.02) * mm, "end": v(957.57, 869.02) * mm});
            skLineSegment(sketch, "E308", {"start": v(957.57, 838.4) * mm, "end": v(1055.37, 838.4) * mm});
            skArc(sketch, "E309", {"start": v(957.57, 869.02) * mm, "mid": v(943.67, 874.71) * mm, "end": v(937.74, 888.52) * mm});
            skArc(sketch, "E310", {"start": v(957.57, 838.4) * mm, "mid": v(921.94, 853.05) * mm, "end": v(906.9, 888.52) * mm});
            skLineSegment(sketch, "E311", {"start": v(937.74, 888.52) * mm, "end": v(936.41, 965.54) * mm});
            skLineSegment(sketch, "E312", {"start": v(936.41, 965.54) * mm, "end": v(906.9, 965.04) * mm});
            skLineSegment(sketch, "E313", {"start": v(906.9, 965.04) * mm, "end": v(906.9, 888.52) * mm});
            skLineSegment(sketch, "E314", {"start": v(1055.37, 1090.15) * mm, "end": v(1106.78, 1079) * mm});
            skLineSegment(sketch, "E315", {"start": v(1106.78, 1079) * mm, "end": v(1106.78, 1069.26) * mm});
            skLineSegment(sketch, "E316", {"start": v(1106.78, 1069.26) * mm, "end": v(1055.37, 1059.52) * mm});
            skLineSegment(sketch, "E317", {"start": v(1055.37, 1090.15) * mm, "end": v(957.57, 1090.15) * mm});
            skLineSegment(sketch, "E318", {"start": v(957.57, 1059.52) * mm, "end": v(1055.37, 1059.52) * mm});
            skArc(sketch, "E319", {"start": v(957.57, 1090.15) * mm, "mid": v(943.67, 1095.84) * mm, "end": v(937.74, 1109.64) * mm});
            skArc(sketch, "E320", {"start": v(957.57, 1059.52) * mm, "mid": v(921.94, 1074.17) * mm, "end": v(906.9, 1109.64) * mm});
            skLineSegment(sketch, "E321", {"start": v(937.74, 1109.64) * mm, "end": v(936.41, 1186.67) * mm});
            skLineSegment(sketch, "E322", {"start": v(936.41, 1186.67) * mm, "end": v(906.9, 1186.16) * mm});
            skLineSegment(sketch, "E323", {"start": v(906.9, 1186.16) * mm, "end": v(906.9, 1109.64) * mm});
            skLineSegment(sketch, "E324", {"start": v(1440.8, 16.02) * mm, "end": v(1492.21, 4.87) * mm});
            skLineSegment(sketch, "E325", {"start": v(1492.21, 4.87) * mm, "end": v(1492.21, -4.87) * mm});
            skLineSegment(sketch, "E326", {"start": v(1492.21, -4.87) * mm, "end": v(1440.8, -14.6) * mm});
            skLineSegment(sketch, "E327", {"start": v(1440.8, 16.02) * mm, "end": v(1343, 16.02) * mm});
            skLineSegment(sketch, "E328", {"start": v(1343, -14.6) * mm, "end": v(1440.8, -14.6) * mm});
            skArc(sketch, "E329", {"start": v(1343, 16.02) * mm, "mid": v(1329.1, 21.71) * mm, "end": v(1323.17, 35.52) * mm});
            skArc(sketch, "E330", {"start": v(1343, -14.6) * mm, "mid": v(1307.37, 0.05) * mm, "end": v(1292.34, 35.52) * mm});
            skLineSegment(sketch, "E331", {"start": v(1323.17, 35.52) * mm, "end": v(1321.84, 112.54) * mm});
            skLineSegment(sketch, "E332", {"start": v(1321.84, 112.54) * mm, "end": v(1292.34, 112.03) * mm});
            skLineSegment(sketch, "E333", {"start": v(1292.34, 112.03) * mm, "end": v(1292.34, 35.52) * mm});
            skLineSegment(sketch, "E334", {"start": v(1440.8, 221.54) * mm, "end": v(1492.21, 210.39) * mm});
            skLineSegment(sketch, "E335", {"start": v(1492.21, 210.39) * mm, "end": v(1492.21, 200.65) * mm});
            skLineSegment(sketch, "E336", {"start": v(1492.21, 200.65) * mm, "end": v(1440.8, 190.92) * mm});
            skLineSegment(sketch, "E337", {"start": v(1440.8, 221.54) * mm, "end": v(1343, 221.54) * mm});
            skLineSegment(sketch, "E338", {"start": v(1343, 190.92) * mm, "end": v(1440.8, 190.92) * mm});
            skArc(sketch, "E339", {"start": v(1343, 221.54) * mm, "mid": v(1329.1, 227.23) * mm, "end": v(1323.17, 241.04) * mm});
            skArc(sketch, "E340", {"start": v(1343, 190.92) * mm, "mid": v(1307.37, 205.56) * mm, "end": v(1292.34, 241.04) * mm});
            skLineSegment(sketch, "E341", {"start": v(1323.17, 241.04) * mm, "end": v(1321.84, 318.06) * mm});
            skLineSegment(sketch, "E342", {"start": v(1321.84, 318.06) * mm, "end": v(1292.34, 317.55) * mm});
            skLineSegment(sketch, "E343", {"start": v(1292.34, 317.55) * mm, "end": v(1292.34, 241.04) * mm});
            skLineSegment(sketch, "E344", {"start": v(1440.8, -187.5) * mm, "end": v(1492.21, -198.65) * mm});
            skLineSegment(sketch, "E345", {"start": v(1492.21, -198.65) * mm, "end": v(1492.21, -208.39) * mm});
            skLineSegment(sketch, "E346", {"start": v(1492.21, -208.39) * mm, "end": v(1440.8, -218.12) * mm});
            skLineSegment(sketch, "E347", {"start": v(1440.8, -187.5) * mm, "end": v(1343, -187.5) * mm});
            skLineSegment(sketch, "E348", {"start": v(1343, -218.12) * mm, "end": v(1440.8, -218.12) * mm});
            skArc(sketch, "E349", {"start": v(1343, -187.5) * mm, "mid": v(1329.1, -181.8) * mm, "end": v(1323.17, -168) * mm});
            skArc(sketch, "E350", {"start": v(1343, -218.12) * mm, "mid": v(1307.37, -203.48) * mm, "end": v(1292.34, -168) * mm});
            skLineSegment(sketch, "E351", {"start": v(1323.17, -168) * mm, "end": v(1321.84, -90.98) * mm});
            skLineSegment(sketch, "E352", {"start": v(1321.84, -90.98) * mm, "end": v(1292.34, -91.49) * mm});
            skLineSegment(sketch, "E353", {"start": v(1292.34, -91.49) * mm, "end": v(1292.34, -168) * mm});
            skLineSegment(sketch, "E354", {"start": v(1440.8, -398.32) * mm, "end": v(1492.21, -409.47) * mm});
            skLineSegment(sketch, "E355", {"start": v(1492.21, -409.47) * mm, "end": v(1492.21, -419.2) * mm});
            skLineSegment(sketch, "E356", {"start": v(1492.21, -419.2) * mm, "end": v(1440.8, -428.94) * mm});
            skLineSegment(sketch, "E357", {"start": v(1440.8, -398.32) * mm, "end": v(1343, -398.32) * mm});
            skLineSegment(sketch, "E358", {"start": v(1343, -428.94) * mm, "end": v(1440.8, -428.94) * mm});
            skArc(sketch, "E359", {"start": v(1343, -398.32) * mm, "mid": v(1329.1, -392.63) * mm, "end": v(1323.17, -378.82) * mm});
            skArc(sketch, "E360", {"start": v(1343, -428.94) * mm, "mid": v(1307.37, -414.3) * mm, "end": v(1292.34, -378.82) * mm});
            skLineSegment(sketch, "E361", {"start": v(1323.17, -378.82) * mm, "end": v(1321.84, -301.8) * mm});
            skLineSegment(sketch, "E362", {"start": v(1321.84, -301.8) * mm, "end": v(1292.34, -302.3) * mm});
            skLineSegment(sketch, "E363", {"start": v(1292.34, -302.3) * mm, "end": v(1292.34, -378.82) * mm});
            skLineSegment(sketch, "E364", {"start": v(1440.8, 429.24) * mm, "end": v(1492.21, 418.08) * mm});
            skLineSegment(sketch, "E365", {"start": v(1492.21, 418.08) * mm, "end": v(1492.21, 408.35) * mm});
            skLineSegment(sketch, "E366", {"start": v(1492.21, 408.35) * mm, "end": v(1440.8, 398.61) * mm});
            skLineSegment(sketch, "E367", {"start": v(1440.8, 429.24) * mm, "end": v(1343, 429.24) * mm});
            skLineSegment(sketch, "E368", {"start": v(1343, 398.61) * mm, "end": v(1440.8, 398.61) * mm});
            skArc(sketch, "E369", {"start": v(1343, 429.24) * mm, "mid": v(1329.1, 434.93) * mm, "end": v(1323.17, 448.73) * mm});
            skArc(sketch, "E370", {"start": v(1343, 398.61) * mm, "mid": v(1307.37, 413.26) * mm, "end": v(1292.34, 448.73) * mm});
            skLineSegment(sketch, "E371", {"start": v(1323.17, 448.73) * mm, "end": v(1321.84, 525.76) * mm});
            skLineSegment(sketch, "E372", {"start": v(1321.84, 525.76) * mm, "end": v(1292.34, 525.25) * mm});
            skLineSegment(sketch, "E373", {"start": v(1292.34, 525.25) * mm, "end": v(1292.34, 448.73) * mm});
            skLineSegment(sketch, "E374", {"start": v(1440.8, 651.7) * mm, "end": v(1492.21, 640.54) * mm});
            skLineSegment(sketch, "E375", {"start": v(1492.21, 640.54) * mm, "end": v(1492.21, 630.8) * mm});
            skLineSegment(sketch, "E376", {"start": v(1492.21, 630.8) * mm, "end": v(1440.8, 621.07) * mm});
            skLineSegment(sketch, "E377", {"start": v(1440.8, 651.7) * mm, "end": v(1343, 651.7) * mm});
            skLineSegment(sketch, "E378", {"start": v(1343, 621.07) * mm, "end": v(1440.8, 621.07) * mm});
            skArc(sketch, "E379", {"start": v(1343, 651.7) * mm, "mid": v(1329.1, 657.39) * mm, "end": v(1323.17, 671.2) * mm});
            skArc(sketch, "E380", {"start": v(1343, 621.07) * mm, "mid": v(1307.37, 635.72) * mm, "end": v(1292.34, 671.2) * mm});
            skLineSegment(sketch, "E381", {"start": v(1323.17, 671.2) * mm, "end": v(1321.84, 748.22) * mm});
            skLineSegment(sketch, "E382", {"start": v(1321.84, 748.22) * mm, "end": v(1292.34, 747.71) * mm});
            skLineSegment(sketch, "E383", {"start": v(1292.34, 747.71) * mm, "end": v(1292.34, 671.2) * mm});
            skLineSegment(sketch, "E384", {"start": v(1440.8, 869.02) * mm, "end": v(1492.21, 857.87) * mm});
            skLineSegment(sketch, "E385", {"start": v(1492.21, 857.87) * mm, "end": v(1492.21, 848.13) * mm});
            skLineSegment(sketch, "E386", {"start": v(1492.21, 848.13) * mm, "end": v(1440.8, 838.4) * mm});
            skLineSegment(sketch, "E387", {"start": v(1440.8, 869.02) * mm, "end": v(1343, 869.02) * mm});
            skLineSegment(sketch, "E388", {"start": v(1343, 838.4) * mm, "end": v(1440.8, 838.4) * mm});
            skArc(sketch, "E389", {"start": v(1343, 869.02) * mm, "mid": v(1329.1, 874.71) * mm, "end": v(1323.17, 888.52) * mm});
            skArc(sketch, "E390", {"start": v(1343, 838.4) * mm, "mid": v(1307.37, 853.05) * mm, "end": v(1292.34, 888.52) * mm});
            skLineSegment(sketch, "E391", {"start": v(1323.17, 888.52) * mm, "end": v(1321.84, 965.54) * mm});
            skLineSegment(sketch, "E392", {"start": v(1321.84, 965.54) * mm, "end": v(1292.34, 965.04) * mm});
            skLineSegment(sketch, "E393", {"start": v(1292.34, 965.04) * mm, "end": v(1292.34, 888.52) * mm});
            skLineSegment(sketch, "E394", {"start": v(1440.8, 1090.15) * mm, "end": v(1492.21, 1079) * mm});
            skLineSegment(sketch, "E395", {"start": v(1492.21, 1079) * mm, "end": v(1492.21, 1069.26) * mm});
            skLineSegment(sketch, "E396", {"start": v(1492.21, 1069.26) * mm, "end": v(1440.8, 1059.52) * mm});
            skLineSegment(sketch, "E397", {"start": v(1440.8, 1090.15) * mm, "end": v(1343, 1090.15) * mm});
            skLineSegment(sketch, "E398", {"start": v(1343, 1059.52) * mm, "end": v(1440.8, 1059.52) * mm});
            skArc(sketch, "E399", {"start": v(1343, 1090.15) * mm, "mid": v(1329.1, 1095.84) * mm, "end": v(1323.17, 1109.64) * mm});
            skArc(sketch, "E400", {"start": v(1343, 1059.52) * mm, "mid": v(1307.37, 1074.17) * mm, "end": v(1292.34, 1109.64) * mm});
            skLineSegment(sketch, "E401", {"start": v(1323.17, 1109.64) * mm, "end": v(1321.84, 1186.67) * mm});
            skLineSegment(sketch, "E402", {"start": v(1321.84, 1186.67) * mm, "end": v(1292.34, 1186.16) * mm});
            skLineSegment(sketch, "E403", {"start": v(1292.34, 1186.16) * mm, "end": v(1292.34, 1109.64) * mm});
            skLineSegment(sketch, "E404", {"start": v(1800.83, 16.02) * mm, "end": v(1852.25, 4.87) * mm});
            skLineSegment(sketch, "E405", {"start": v(1852.25, 4.87) * mm, "end": v(1852.25, -4.87) * mm});
            skLineSegment(sketch, "E406", {"start": v(1852.25, -4.87) * mm, "end": v(1800.83, -14.6) * mm});
            skLineSegment(sketch, "E407", {"start": v(1800.83, 16.02) * mm, "end": v(1703.03, 16.02) * mm});
            skLineSegment(sketch, "E408", {"start": v(1703.03, -14.6) * mm, "end": v(1800.83, -14.6) * mm});
            skArc(sketch, "E409", {"start": v(1703.03, 16.02) * mm, "mid": v(1689.13, 21.71) * mm, "end": v(1683.2, 35.52) * mm});
            skArc(sketch, "E410", {"start": v(1703.03, -14.6) * mm, "mid": v(1667.4, 0.05) * mm, "end": v(1652.37, 35.52) * mm});
            skLineSegment(sketch, "E411", {"start": v(1683.2, 35.52) * mm, "end": v(1681.88, 112.54) * mm});
            skLineSegment(sketch, "E412", {"start": v(1681.88, 112.54) * mm, "end": v(1652.37, 112.03) * mm});
            skLineSegment(sketch, "E413", {"start": v(1652.37, 112.03) * mm, "end": v(1652.37, 35.52) * mm});
            skLineSegment(sketch, "E414", {"start": v(1800.83, 221.54) * mm, "end": v(1852.25, 210.39) * mm});
            skLineSegment(sketch, "E415", {"start": v(1852.25, 210.39) * mm, "end": v(1852.25, 200.65) * mm});
            skLineSegment(sketch, "E416", {"start": v(1852.25, 200.65) * mm, "end": v(1800.83, 190.92) * mm});
            skLineSegment(sketch, "E417", {"start": v(1800.83, 221.54) * mm, "end": v(1703.03, 221.54) * mm});
            skLineSegment(sketch, "E418", {"start": v(1703.03, 190.92) * mm, "end": v(1800.83, 190.92) * mm});
            skArc(sketch, "E419", {"start": v(1703.03, 221.54) * mm, "mid": v(1689.13, 227.23) * mm, "end": v(1683.2, 241.04) * mm});
            skArc(sketch, "E420", {"start": v(1703.03, 190.92) * mm, "mid": v(1667.4, 205.56) * mm, "end": v(1652.37, 241.04) * mm});
            skLineSegment(sketch, "E421", {"start": v(1683.2, 241.04) * mm, "end": v(1681.88, 318.06) * mm});
            skLineSegment(sketch, "E422", {"start": v(1681.88, 318.06) * mm, "end": v(1652.37, 317.55) * mm});
            skLineSegment(sketch, "E423", {"start": v(1652.37, 317.55) * mm, "end": v(1652.37, 241.04) * mm});
            skLineSegment(sketch, "E424", {"start": v(1800.83, -187.5) * mm, "end": v(1852.25, -198.65) * mm});
            skLineSegment(sketch, "E425", {"start": v(1852.25, -198.65) * mm, "end": v(1852.25, -208.39) * mm});
            skLineSegment(sketch, "E426", {"start": v(1852.25, -208.39) * mm, "end": v(1800.83, -218.12) * mm});
            skLineSegment(sketch, "E427", {"start": v(1800.83, -187.5) * mm, "end": v(1703.03, -187.5) * mm});
            skLineSegment(sketch, "E428", {"start": v(1703.03, -218.12) * mm, "end": v(1800.83, -218.12) * mm});
            skArc(sketch, "E429", {"start": v(1703.03, -187.5) * mm, "mid": v(1689.13, -181.8) * mm, "end": v(1683.2, -168) * mm});
            skArc(sketch, "E430", {"start": v(1703.03, -218.12) * mm, "mid": v(1667.4, -203.48) * mm, "end": v(1652.37, -168) * mm});
            skLineSegment(sketch, "E431", {"start": v(1683.2, -168) * mm, "end": v(1681.88, -90.98) * mm});
            skLineSegment(sketch, "E432", {"start": v(1681.88, -90.98) * mm, "end": v(1652.37, -91.49) * mm});
            skLineSegment(sketch, "E433", {"start": v(1652.37, -91.49) * mm, "end": v(1652.37, -168) * mm});
            skLineSegment(sketch, "E434", {"start": v(1800.83, -398.32) * mm, "end": v(1852.25, -409.47) * mm});
            skLineSegment(sketch, "E435", {"start": v(1852.25, -409.47) * mm, "end": v(1852.25, -419.2) * mm});
            skLineSegment(sketch, "E436", {"start": v(1852.25, -419.2) * mm, "end": v(1800.83, -428.94) * mm});
            skLineSegment(sketch, "E437", {"start": v(1800.83, -398.32) * mm, "end": v(1703.03, -398.32) * mm});
            skLineSegment(sketch, "E438", {"start": v(1703.03, -428.94) * mm, "end": v(1800.83, -428.94) * mm});
            skArc(sketch, "E439", {"start": v(1703.03, -398.32) * mm, "mid": v(1689.13, -392.63) * mm, "end": v(1683.2, -378.82) * mm});
            skArc(sketch, "E440", {"start": v(1703.03, -428.94) * mm, "mid": v(1667.4, -414.3) * mm, "end": v(1652.37, -378.82) * mm});
            skLineSegment(sketch, "E441", {"start": v(1683.2, -378.82) * mm, "end": v(1681.88, -301.8) * mm});
            skLineSegment(sketch, "E442", {"start": v(1681.88, -301.8) * mm, "end": v(1652.37, -302.3) * mm});
            skLineSegment(sketch, "E443", {"start": v(1652.37, -302.3) * mm, "end": v(1652.37, -378.82) * mm});
            skLineSegment(sketch, "E444", {"start": v(1800.83, 429.24) * mm, "end": v(1852.25, 418.08) * mm});
            skLineSegment(sketch, "E445", {"start": v(1852.25, 418.08) * mm, "end": v(1852.25, 408.35) * mm});
            skLineSegment(sketch, "E446", {"start": v(1852.25, 408.35) * mm, "end": v(1800.83, 398.61) * mm});
            skLineSegment(sketch, "E447", {"start": v(1800.83, 429.24) * mm, "end": v(1703.03, 429.24) * mm});
            skLineSegment(sketch, "E448", {"start": v(1703.03, 398.61) * mm, "end": v(1800.83, 398.61) * mm});
            skArc(sketch, "E449", {"start": v(1703.03, 429.24) * mm, "mid": v(1689.13, 434.93) * mm, "end": v(1683.2, 448.73) * mm});
            skArc(sketch, "E450", {"start": v(1703.03, 398.61) * mm, "mid": v(1667.4, 413.26) * mm, "end": v(1652.37, 448.73) * mm});
            skLineSegment(sketch, "E451", {"start": v(1683.2, 448.73) * mm, "end": v(1681.88, 525.76) * mm});
            skLineSegment(sketch, "E452", {"start": v(1681.88, 525.76) * mm, "end": v(1652.37, 525.25) * mm});
            skLineSegment(sketch, "E453", {"start": v(1652.37, 525.25) * mm, "end": v(1652.37, 448.73) * mm});
            skLineSegment(sketch, "E454", {"start": v(1800.83, 651.7) * mm, "end": v(1852.25, 640.54) * mm});
            skLineSegment(sketch, "E455", {"start": v(1852.25, 640.54) * mm, "end": v(1852.25, 630.8) * mm});
            skLineSegment(sketch, "E456", {"start": v(1852.25, 630.8) * mm, "end": v(1800.83, 621.07) * mm});
            skLineSegment(sketch, "E457", {"start": v(1800.83, 651.7) * mm, "end": v(1703.03, 651.7) * mm});
            skLineSegment(sketch, "E458", {"start": v(1703.03, 621.07) * mm, "end": v(1800.83, 621.07) * mm});
            skArc(sketch, "E459", {"start": v(1703.03, 651.7) * mm, "mid": v(1689.13, 657.39) * mm, "end": v(1683.2, 671.2) * mm});
            skArc(sketch, "E460", {"start": v(1703.03, 621.07) * mm, "mid": v(1667.4, 635.72) * mm, "end": v(1652.37, 671.2) * mm});
            skLineSegment(sketch, "E461", {"start": v(1683.2, 671.2) * mm, "end": v(1681.88, 748.22) * mm});
            skLineSegment(sketch, "E462", {"start": v(1681.88, 748.22) * mm, "end": v(1652.37, 747.71) * mm});
            skLineSegment(sketch, "E463", {"start": v(1652.37, 747.71) * mm, "end": v(1652.37, 671.2) * mm});
            skLineSegment(sketch, "E464", {"start": v(1800.83, 869.02) * mm, "end": v(1852.25, 857.87) * mm});
            skLineSegment(sketch, "E465", {"start": v(1852.25, 857.87) * mm, "end": v(1852.25, 848.13) * mm});
            skLineSegment(sketch, "E466", {"start": v(1852.25, 848.13) * mm, "end": v(1800.83, 838.4) * mm});
            skLineSegment(sketch, "E467", {"start": v(1800.83, 869.02) * mm, "end": v(1703.03, 869.02) * mm});
            skLineSegment(sketch, "E468", {"start": v(1703.03, 838.4) * mm, "end": v(1800.83, 838.4) * mm});
            skArc(sketch, "E469", {"start": v(1703.03, 869.02) * mm, "mid": v(1689.13, 874.71) * mm, "end": v(1683.2, 888.52) * mm});
            skArc(sketch, "E470", {"start": v(1703.03, 838.4) * mm, "mid": v(1667.4, 853.05) * mm, "end": v(1652.37, 888.52) * mm});
            skLineSegment(sketch, "E471", {"start": v(1683.2, 888.52) * mm, "end": v(1681.88, 965.54) * mm});
            skLineSegment(sketch, "E472", {"start": v(1681.88, 965.54) * mm, "end": v(1652.37, 965.04) * mm});
            skLineSegment(sketch, "E473", {"start": v(1652.37, 965.04) * mm, "end": v(1652.37, 888.52) * mm});
            skLineSegment(sketch, "E474", {"start": v(1800.83, 1090.15) * mm, "end": v(1852.25, 1079) * mm});
            skLineSegment(sketch, "E475", {"start": v(1852.25, 1079) * mm, "end": v(1852.25, 1069.26) * mm});
            skLineSegment(sketch, "E476", {"start": v(1852.25, 1069.26) * mm, "end": v(1800.83, 1059.52) * mm});
            skLineSegment(sketch, "E477", {"start": v(1800.83, 1090.15) * mm, "end": v(1703.03, 1090.15) * mm});
            skLineSegment(sketch, "E478", {"start": v(1703.03, 1059.52) * mm, "end": v(1800.83, 1059.52) * mm});
            skArc(sketch, "E479", {"start": v(1703.03, 1090.15) * mm, "mid": v(1689.13, 1095.84) * mm, "end": v(1683.2, 1109.64) * mm});
            skArc(sketch, "E480", {"start": v(1703.03, 1059.52) * mm, "mid": v(1667.4, 1074.17) * mm, "end": v(1652.37, 1109.64) * mm});
            skLineSegment(sketch, "E481", {"start": v(1683.2, 1109.64) * mm, "end": v(1681.88, 1186.67) * mm});
            skLineSegment(sketch, "E482", {"start": v(1681.88, 1186.67) * mm, "end": v(1652.37, 1186.16) * mm});
            skLineSegment(sketch, "E483", {"start": v(1652.37, 1186.16) * mm, "end": v(1652.37, 1109.64) * mm});
            skLineSegment(sketch, "E484", {"start": v(2187.55, 16.02) * mm, "end": v(2238.97, 4.87) * mm});
            skLineSegment(sketch, "E485", {"start": v(2238.97, 4.87) * mm, "end": v(2238.97, -4.87) * mm});
            skLineSegment(sketch, "E486", {"start": v(2238.97, -4.87) * mm, "end": v(2187.55, -14.6) * mm});
            skLineSegment(sketch, "E487", {"start": v(2187.55, 16.02) * mm, "end": v(2089.75, 16.02) * mm});
            skLineSegment(sketch, "E488", {"start": v(2089.75, -14.6) * mm, "end": v(2187.55, -14.6) * mm});
            skArc(sketch, "E489", {"start": v(2089.75, 16.02) * mm, "mid": v(2075.85, 21.71) * mm, "end": v(2069.92, 35.52) * mm});
            skArc(sketch, "E490", {"start": v(2089.75, -14.6) * mm, "mid": v(2054.12, 0.05) * mm, "end": v(2039.1, 35.52) * mm});
            skLineSegment(sketch, "E491", {"start": v(2069.92, 35.52) * mm, "end": v(2068.6, 112.54) * mm});
            skLineSegment(sketch, "E492", {"start": v(2068.6, 112.54) * mm, "end": v(2039.1, 112.03) * mm});
            skLineSegment(sketch, "E493", {"start": v(2039.1, 112.03) * mm, "end": v(2039.1, 35.52) * mm});
            skLineSegment(sketch, "E494", {"start": v(2187.55, 221.54) * mm, "end": v(2238.97, 210.39) * mm});
            skLineSegment(sketch, "E495", {"start": v(2238.97, 210.39) * mm, "end": v(2238.97, 200.65) * mm});
            skLineSegment(sketch, "E496", {"start": v(2238.97, 200.65) * mm, "end": v(2187.55, 190.92) * mm});
            skLineSegment(sketch, "E497", {"start": v(2187.55, 221.54) * mm, "end": v(2089.75, 221.54) * mm});
            skLineSegment(sketch, "E498", {"start": v(2089.75, 190.92) * mm, "end": v(2187.55, 190.92) * mm});
            skArc(sketch, "E499", {"start": v(2089.75, 221.54) * mm, "mid": v(2075.85, 227.23) * mm, "end": v(2069.92, 241.04) * mm});
            skArc(sketch, "E500", {"start": v(2089.75, 190.92) * mm, "mid": v(2054.12, 205.56) * mm, "end": v(2039.1, 241.04) * mm});
            skLineSegment(sketch, "E501", {"start": v(2069.92, 241.04) * mm, "end": v(2068.6, 318.06) * mm});
            skLineSegment(sketch, "E502", {"start": v(2068.6, 318.06) * mm, "end": v(2039.1, 317.55) * mm});
            skLineSegment(sketch, "E503", {"start": v(2039.1, 317.55) * mm, "end": v(2039.1, 241.04) * mm});
            skLineSegment(sketch, "E504", {"start": v(2187.55, -187.5) * mm, "end": v(2238.97, -198.65) * mm});
            skLineSegment(sketch, "E505", {"start": v(2238.97, -198.65) * mm, "end": v(2238.97, -208.39) * mm});
            skLineSegment(sketch, "E506", {"start": v(2238.97, -208.39) * mm, "end": v(2187.55, -218.12) * mm});
            skLineSegment(sketch, "E507", {"start": v(2187.55, -187.5) * mm, "end": v(2089.75, -187.5) * mm});
            skLineSegment(sketch, "E508", {"start": v(2089.75, -218.12) * mm, "end": v(2187.55, -218.12) * mm});
            skArc(sketch, "E509", {"start": v(2089.75, -187.5) * mm, "mid": v(2075.85, -181.8) * mm, "end": v(2069.92, -168) * mm});
            skArc(sketch, "E510", {"start": v(2089.75, -218.12) * mm, "mid": v(2054.12, -203.48) * mm, "end": v(2039.1, -168) * mm});
            skLineSegment(sketch, "E511", {"start": v(2069.92, -168) * mm, "end": v(2068.6, -90.98) * mm});
            skLineSegment(sketch, "E512", {"start": v(2068.6, -90.98) * mm, "end": v(2039.1, -91.49) * mm});
            skLineSegment(sketch, "E513", {"start": v(2039.1, -91.49) * mm, "end": v(2039.1, -168) * mm});
            skLineSegment(sketch, "E514", {"start": v(2187.55, -398.32) * mm, "end": v(2238.97, -409.47) * mm});
            skLineSegment(sketch, "E515", {"start": v(2238.97, -409.47) * mm, "end": v(2238.97, -419.2) * mm});
            skLineSegment(sketch, "E516", {"start": v(2238.97, -419.2) * mm, "end": v(2187.55, -428.94) * mm});
            skLineSegment(sketch, "E517", {"start": v(2187.55, -398.32) * mm, "end": v(2089.75, -398.32) * mm});
            skLineSegment(sketch, "E518", {"start": v(2089.75, -428.94) * mm, "end": v(2187.55, -428.94) * mm});
            skArc(sketch, "E519", {"start": v(2089.75, -398.32) * mm, "mid": v(2075.85, -392.63) * mm, "end": v(2069.92, -378.82) * mm});
            skArc(sketch, "E520", {"start": v(2089.75, -428.94) * mm, "mid": v(2054.12, -414.3) * mm, "end": v(2039.1, -378.82) * mm});
            skLineSegment(sketch, "E521", {"start": v(2069.92, -378.82) * mm, "end": v(2068.6, -301.8) * mm});
            skLineSegment(sketch, "E522", {"start": v(2068.6, -301.8) * mm, "end": v(2039.1, -302.3) * mm});
            skLineSegment(sketch, "E523", {"start": v(2039.1, -302.3) * mm, "end": v(2039.1, -378.82) * mm});
            skLineSegment(sketch, "E524", {"start": v(2187.55, 429.24) * mm, "end": v(2238.97, 418.08) * mm});
            skLineSegment(sketch, "E525", {"start": v(2238.97, 418.08) * mm, "end": v(2238.97, 408.35) * mm});
            skLineSegment(sketch, "E526", {"start": v(2238.97, 408.35) * mm, "end": v(2187.55, 398.61) * mm});
            skLineSegment(sketch, "E527", {"start": v(2187.55, 429.24) * mm, "end": v(2089.75, 429.24) * mm});
            skLineSegment(sketch, "E528", {"start": v(2089.75, 398.61) * mm, "end": v(2187.55, 398.61) * mm});
            skArc(sketch, "E529", {"start": v(2089.75, 429.24) * mm, "mid": v(2075.85, 434.93) * mm, "end": v(2069.92, 448.73) * mm});
            skArc(sketch, "E530", {"start": v(2089.75, 398.61) * mm, "mid": v(2054.12, 413.26) * mm, "end": v(2039.1, 448.73) * mm});
            skLineSegment(sketch, "E531", {"start": v(2069.92, 448.73) * mm, "end": v(2068.6, 525.76) * mm});
            skLineSegment(sketch, "E532", {"start": v(2068.6, 525.76) * mm, "end": v(2039.1, 525.25) * mm});
            skLineSegment(sketch, "E533", {"start": v(2039.1, 525.25) * mm, "end": v(2039.1, 448.73) * mm});
            skLineSegment(sketch, "E534", {"start": v(2187.55, 651.7) * mm, "end": v(2238.97, 640.54) * mm});
            skLineSegment(sketch, "E535", {"start": v(2238.97, 640.54) * mm, "end": v(2238.97, 630.8) * mm});
            skLineSegment(sketch, "E536", {"start": v(2238.97, 630.8) * mm, "end": v(2187.55, 621.07) * mm});
            skLineSegment(sketch, "E537", {"start": v(2187.55, 651.7) * mm, "end": v(2089.75, 651.7) * mm});
            skLineSegment(sketch, "E538", {"start": v(2089.75, 621.07) * mm, "end": v(2187.55, 621.07) * mm});
            skArc(sketch, "E539", {"start": v(2089.75, 651.7) * mm, "mid": v(2075.85, 657.39) * mm, "end": v(2069.92, 671.2) * mm});
            skArc(sketch, "E540", {"start": v(2089.75, 621.07) * mm, "mid": v(2054.12, 635.72) * mm, "end": v(2039.1, 671.2) * mm});
            skLineSegment(sketch, "E541", {"start": v(2069.92, 671.2) * mm, "end": v(2068.6, 748.22) * mm});
            skLineSegment(sketch, "E542", {"start": v(2068.6, 748.22) * mm, "end": v(2039.1, 747.71) * mm});
            skLineSegment(sketch, "E543", {"start": v(2039.1, 747.71) * mm, "end": v(2039.1, 671.2) * mm});
            skLineSegment(sketch, "E544", {"start": v(2187.55, 869.02) * mm, "end": v(2238.97, 857.87) * mm});
            skLineSegment(sketch, "E545", {"start": v(2238.97, 857.87) * mm, "end": v(2238.97, 848.13) * mm});
            skLineSegment(sketch, "E546", {"start": v(2238.97, 848.13) * mm, "end": v(2187.55, 838.4) * mm});
            skLineSegment(sketch, "E547", {"start": v(2187.55, 869.02) * mm, "end": v(2089.75, 869.02) * mm});
            skLineSegment(sketch, "E548", {"start": v(2089.75, 838.4) * mm, "end": v(2187.55, 838.4) * mm});
            skArc(sketch, "E549", {"start": v(2089.75, 869.02) * mm, "mid": v(2075.85, 874.71) * mm, "end": v(2069.92, 888.52) * mm});
            skArc(sketch, "E550", {"start": v(2089.75, 838.4) * mm, "mid": v(2054.12, 853.05) * mm, "end": v(2039.1, 888.52) * mm});
            skLineSegment(sketch, "E551", {"start": v(2069.92, 888.52) * mm, "end": v(2068.6, 965.54) * mm});
            skLineSegment(sketch, "E552", {"start": v(2068.6, 965.54) * mm, "end": v(2039.1, 965.04) * mm});
            skLineSegment(sketch, "E553", {"start": v(2039.1, 965.04) * mm, "end": v(2039.1, 888.52) * mm});
            skLineSegment(sketch, "E554", {"start": v(2187.55, 1090.15) * mm, "end": v(2238.97, 1079) * mm});
            skLineSegment(sketch, "E555", {"start": v(2238.97, 1079) * mm, "end": v(2238.97, 1069.26) * mm});
            skLineSegment(sketch, "E556", {"start": v(2238.97, 1069.26) * mm, "end": v(2187.55, 1059.52) * mm});
            skLineSegment(sketch, "E557", {"start": v(2187.55, 1090.15) * mm, "end": v(2089.75, 1090.15) * mm});
            skLineSegment(sketch, "E558", {"start": v(2089.75, 1059.52) * mm, "end": v(2187.55, 1059.52) * mm});
            skArc(sketch, "E559", {"start": v(2089.75, 1090.15) * mm, "mid": v(2075.85, 1095.84) * mm, "end": v(2069.92, 1109.64) * mm});
            skArc(sketch, "E560", {"start": v(2089.75, 1059.52) * mm, "mid": v(2054.12, 1074.17) * mm, "end": v(2039.1, 1109.64) * mm});
            skLineSegment(sketch, "E561", {"start": v(2069.92, 1109.64) * mm, "end": v(2068.6, 1186.67) * mm});
            skLineSegment(sketch, "E562", {"start": v(2068.6, 1186.67) * mm, "end": v(2039.1, 1186.16) * mm});
            skLineSegment(sketch, "E563", {"start": v(2039.1, 1186.16) * mm, "end": v(2039.1, 1109.64) * mm});
            skLineSegment(sketch, "E564", {"start": v(2547.58, 16.02) * mm, "end": v(2599, 4.87) * mm});
            skLineSegment(sketch, "E565", {"start": v(2599, 4.87) * mm, "end": v(2599, -4.87) * mm});
            skLineSegment(sketch, "E566", {"start": v(2599, -4.87) * mm, "end": v(2547.58, -14.6) * mm});
            skLineSegment(sketch, "E567", {"start": v(2547.58, 16.02) * mm, "end": v(2449.79, 16.02) * mm});
            skLineSegment(sketch, "E568", {"start": v(2449.79, -14.6) * mm, "end": v(2547.58, -14.6) * mm});
            skArc(sketch, "E569", {"start": v(2449.79, 16.02) * mm, "mid": v(2435.88, 21.71) * mm, "end": v(2429.95, 35.52) * mm});
            skArc(sketch, "E570", {"start": v(2449.79, -14.6) * mm, "mid": v(2414.15, 0.05) * mm, "end": v(2399.12, 35.52) * mm});
            skLineSegment(sketch, "E571", {"start": v(2429.95, 35.52) * mm, "end": v(2428.63, 112.54) * mm});
            skLineSegment(sketch, "E572", {"start": v(2428.63, 112.54) * mm, "end": v(2399.12, 112.03) * mm});
            skLineSegment(sketch, "E573", {"start": v(2399.12, 112.03) * mm, "end": v(2399.12, 35.52) * mm});
            skLineSegment(sketch, "E574", {"start": v(2547.58, 221.54) * mm, "end": v(2599, 210.39) * mm});
            skLineSegment(sketch, "E575", {"start": v(2599, 210.39) * mm, "end": v(2599, 200.65) * mm});
            skLineSegment(sketch, "E576", {"start": v(2599, 200.65) * mm, "end": v(2547.58, 190.92) * mm});
            skLineSegment(sketch, "E577", {"start": v(2547.58, 221.54) * mm, "end": v(2449.79, 221.54) * mm});
            skLineSegment(sketch, "E578", {"start": v(2449.79, 190.92) * mm, "end": v(2547.58, 190.92) * mm});
            skArc(sketch, "E579", {"start": v(2449.79, 221.54) * mm, "mid": v(2435.88, 227.23) * mm, "end": v(2429.95, 241.04) * mm});
            skArc(sketch, "E580", {"start": v(2449.79, 190.92) * mm, "mid": v(2414.15, 205.56) * mm, "end": v(2399.12, 241.04) * mm});
            skLineSegment(sketch, "E581", {"start": v(2429.95, 241.04) * mm, "end": v(2428.63, 318.06) * mm});
            skLineSegment(sketch, "E582", {"start": v(2428.63, 318.06) * mm, "end": v(2399.12, 317.55) * mm});
            skLineSegment(sketch, "E583", {"start": v(2399.12, 317.55) * mm, "end": v(2399.12, 241.04) * mm});
            skLineSegment(sketch, "E584", {"start": v(2547.58, -187.5) * mm, "end": v(2599, -198.65) * mm});
            skLineSegment(sketch, "E585", {"start": v(2599, -198.65) * mm, "end": v(2599, -208.39) * mm});
            skLineSegment(sketch, "E586", {"start": v(2599, -208.39) * mm, "end": v(2547.58, -218.12) * mm});
            skLineSegment(sketch, "E587", {"start": v(2547.58, -187.5) * mm, "end": v(2449.79, -187.5) * mm});
            skLineSegment(sketch, "E588", {"start": v(2449.79, -218.12) * mm, "end": v(2547.58, -218.12) * mm});
            skArc(sketch, "E589", {"start": v(2449.79, -187.5) * mm, "mid": v(2435.88, -181.8) * mm, "end": v(2429.95, -168) * mm});
            skArc(sketch, "E590", {"start": v(2449.79, -218.12) * mm, "mid": v(2414.15, -203.48) * mm, "end": v(2399.12, -168) * mm});
            skLineSegment(sketch, "E591", {"start": v(2429.95, -168) * mm, "end": v(2428.63, -90.98) * mm});
            skLineSegment(sketch, "E592", {"start": v(2428.63, -90.98) * mm, "end": v(2399.12, -91.49) * mm});
            skLineSegment(sketch, "E593", {"start": v(2399.12, -91.49) * mm, "end": v(2399.12, -168) * mm});
            skLineSegment(sketch, "E594", {"start": v(2547.58, -398.32) * mm, "end": v(2599, -409.47) * mm});
            skLineSegment(sketch, "E595", {"start": v(2599, -409.47) * mm, "end": v(2599, -419.2) * mm});
            skLineSegment(sketch, "E596", {"start": v(2599, -419.2) * mm, "end": v(2547.58, -428.94) * mm});
            skLineSegment(sketch, "E597", {"start": v(2547.58, -398.32) * mm, "end": v(2449.79, -398.32) * mm});
            skLineSegment(sketch, "E598", {"start": v(2449.79, -428.94) * mm, "end": v(2547.58, -428.94) * mm});
            skArc(sketch, "E599", {"start": v(2449.79, -398.32) * mm, "mid": v(2435.88, -392.63) * mm, "end": v(2429.95, -378.82) * mm});
            skArc(sketch, "E600", {"start": v(2449.79, -428.94) * mm, "mid": v(2414.15, -414.3) * mm, "end": v(2399.12, -378.82) * mm});
            skLineSegment(sketch, "E601", {"start": v(2429.95, -378.82) * mm, "end": v(2428.63, -301.8) * mm});
            skLineSegment(sketch, "E602", {"start": v(2428.63, -301.8) * mm, "end": v(2399.12, -302.3) * mm});
            skLineSegment(sketch, "E603", {"start": v(2399.12, -302.3) * mm, "end": v(2399.12, -378.82) * mm});
            skLineSegment(sketch, "E604", {"start": v(2547.58, 429.24) * mm, "end": v(2599, 418.08) * mm});
            skLineSegment(sketch, "E605", {"start": v(2599, 418.08) * mm, "end": v(2599, 408.35) * mm});
            skLineSegment(sketch, "E606", {"start": v(2599, 408.35) * mm, "end": v(2547.58, 398.61) * mm});
            skLineSegment(sketch, "E607", {"start": v(2547.58, 429.24) * mm, "end": v(2449.79, 429.24) * mm});
            skLineSegment(sketch, "E608", {"start": v(2449.79, 398.61) * mm, "end": v(2547.58, 398.61) * mm});
            skArc(sketch, "E609", {"start": v(2449.79, 429.24) * mm, "mid": v(2435.88, 434.93) * mm, "end": v(2429.95, 448.73) * mm});
            skArc(sketch, "E610", {"start": v(2449.79, 398.61) * mm, "mid": v(2414.15, 413.26) * mm, "end": v(2399.12, 448.73) * mm});
            skLineSegment(sketch, "E611", {"start": v(2429.95, 448.73) * mm, "end": v(2428.63, 525.76) * mm});
            skLineSegment(sketch, "E612", {"start": v(2428.63, 525.76) * mm, "end": v(2399.12, 525.25) * mm});
            skLineSegment(sketch, "E613", {"start": v(2399.12, 525.25) * mm, "end": v(2399.12, 448.73) * mm});
            skLineSegment(sketch, "E614", {"start": v(2547.58, 651.7) * mm, "end": v(2599, 640.54) * mm});
            skLineSegment(sketch, "E615", {"start": v(2599, 640.54) * mm, "end": v(2599, 630.8) * mm});
            skLineSegment(sketch, "E616", {"start": v(2599, 630.8) * mm, "end": v(2547.58, 621.07) * mm});
            skLineSegment(sketch, "E617", {"start": v(2547.58, 651.7) * mm, "end": v(2449.79, 651.7) * mm});
            skLineSegment(sketch, "E618", {"start": v(2449.79, 621.07) * mm, "end": v(2547.58, 621.07) * mm});
            skArc(sketch, "E619", {"start": v(2449.79, 651.7) * mm, "mid": v(2435.88, 657.39) * mm, "end": v(2429.95, 671.2) * mm});
            skArc(sketch, "E620", {"start": v(2449.79, 621.07) * mm, "mid": v(2414.15, 635.72) * mm, "end": v(2399.12, 671.2) * mm});
            skLineSegment(sketch, "E621", {"start": v(2429.95, 671.2) * mm, "end": v(2428.63, 748.22) * mm});
            skLineSegment(sketch, "E622", {"start": v(2428.63, 748.22) * mm, "end": v(2399.12, 747.71) * mm});
            skLineSegment(sketch, "E623", {"start": v(2399.12, 747.71) * mm, "end": v(2399.12, 671.2) * mm});
            skLineSegment(sketch, "E624", {"start": v(2547.58, 869.02) * mm, "end": v(2599, 857.87) * mm});
            skLineSegment(sketch, "E625", {"start": v(2599, 857.87) * mm, "end": v(2599, 848.13) * mm});
            skLineSegment(sketch, "E626", {"start": v(2599, 848.13) * mm, "end": v(2547.58, 838.4) * mm});
            skLineSegment(sketch, "E627", {"start": v(2547.58, 869.02) * mm, "end": v(2449.79, 869.02) * mm});
            skLineSegment(sketch, "E628", {"start": v(2449.79, 838.4) * mm, "end": v(2547.58, 838.4) * mm});
            skArc(sketch, "E629", {"start": v(2449.79, 869.02) * mm, "mid": v(2435.88, 874.71) * mm, "end": v(2429.95, 888.52) * mm});
            skArc(sketch, "E630", {"start": v(2449.79, 838.4) * mm, "mid": v(2414.15, 853.05) * mm, "end": v(2399.12, 888.52) * mm});
            skLineSegment(sketch, "E631", {"start": v(2429.95, 888.52) * mm, "end": v(2428.63, 965.54) * mm});
            skLineSegment(sketch, "E632", {"start": v(2428.63, 965.54) * mm, "end": v(2399.12, 965.04) * mm});
            skLineSegment(sketch, "E633", {"start": v(2399.12, 965.04) * mm, "end": v(2399.12, 888.52) * mm});
            skLineSegment(sketch, "E634", {"start": v(2547.58, 1090.15) * mm, "end": v(2599, 1079) * mm});
            skLineSegment(sketch, "E635", {"start": v(2599, 1079) * mm, "end": v(2599, 1069.26) * mm});
            skLineSegment(sketch, "E636", {"start": v(2599, 1069.26) * mm, "end": v(2547.58, 1059.52) * mm});
            skLineSegment(sketch, "E637", {"start": v(2547.58, 1090.15) * mm, "end": v(2449.79, 1090.15) * mm});
            skLineSegment(sketch, "E638", {"start": v(2449.79, 1059.52) * mm, "end": v(2547.58, 1059.52) * mm});
            skArc(sketch, "E639", {"start": v(2449.79, 1090.15) * mm, "mid": v(2435.88, 1095.84) * mm, "end": v(2429.95, 1109.64) * mm});
            skArc(sketch, "E640", {"start": v(2449.79, 1059.52) * mm, "mid": v(2414.15, 1074.17) * mm, "end": v(2399.12, 1109.64) * mm});
            skLineSegment(sketch, "E641", {"start": v(2429.95, 1109.64) * mm, "end": v(2428.63, 1186.67) * mm});
            skLineSegment(sketch, "E642", {"start": v(2428.63, 1186.67) * mm, "end": v(2399.12, 1186.16) * mm});
            skLineSegment(sketch, "E643", {"start": v(2399.12, 1186.16) * mm, "end": v(2399.12, 1109.64) * mm});
            skSolve(sketch);
        }
        {
            var Q0;
            Q0=qSketchRegion(id+"F2",true);
            extrude(context, id + "F3", {"entities" : qUnion([Q0]), "depth" : 10.16 * mm, "offsetDistance" : 25.4 * mm});
        }
        {
            var Q0;
            Q0=makeQuery(id+"F3.opExtrude","CAP_FACE",FACE,{"disambiguationData":[OSD([sQuery(id+"F2.wireOp",EDGE,"E4"),sQuery(id+"F2.wireOp",EDGE,"E5"),sQuery(id+"F2.wireOp",EDGE,"E6"),sQuery(id+"F2.wireOp",EDGE,"E7"),sQuery(id+"F2.wireOp",EDGE,"JgvzJjwD-TXg6-fWbI-FKHk-LL5GRCbPJZjB"),sQuery(id+"F2.wireOp",EDGE,"E8")])],"isStart":false});
            var sketch = newSketch(context, id + "F4", { "sketchPlane" : qUnion([Q0])});
            skLineSegment(sketch, "E644", {"start": v(-51.41, 16.02) * mm, "end": v(0, 4.87) * mm});
            skLineSegment(sketch, "E645", {"start": v(0, 4.87) * mm, "end": v(0, -4.87) * mm});
            skLineSegment(sketch, "E646", {"start": v(0, -4.87) * mm, "end": v(-51.41, -14.6) * mm});
            skLineSegment(sketch, "E647", {"start": v(-51.41, -14.6) * mm, "end": v(-51.41, 16.02) * mm});
            skLineSegment(sketch, "E648", {"start": v(-51.41, -187.57) * mm, "end": v(-0.18, -198.68) * mm});
            skLineSegment(sketch, "E649", {"start": v(-0.18, -198.68) * mm, "end": v(-0.18, -208.36) * mm});
            skLineSegment(sketch, "E650", {"start": v(-0.18, -208.36) * mm, "end": v(-51.41, -218.18) * mm});
            skLineSegment(sketch, "E651", {"start": v(-51.41, -218.18) * mm, "end": v(-51.41, -187.57) * mm});
            skLineSegment(sketch, "E652", {"start": v(-51.46, -398.32) * mm, "end": v(-0.24, -409.45) * mm});
            skLineSegment(sketch, "E653", {"start": v(-0.24, -409.45) * mm, "end": v(-0.24, -418.83) * mm});
            skLineSegment(sketch, "E654", {"start": v(-0.24, -418.83) * mm, "end": v(-51.67, -428.97) * mm});
            skLineSegment(sketch, "E655", {"start": v(-51.67, -428.97) * mm, "end": v(-51.46, -398.32) * mm});
            skLineSegment(sketch, "E656", {"start": v(-51.41, 190.93) * mm, "end": v(-0.1, 200.7) * mm});
            skLineSegment(sketch, "E657", {"start": v(-0.1, 200.7) * mm, "end": v(-0.1, 210.4) * mm});
            skLineSegment(sketch, "E658", {"start": v(-0.1, 210.4) * mm, "end": v(-51.48, 221.6) * mm});
            skLineSegment(sketch, "E659", {"start": v(-51.48, 221.6) * mm, "end": v(-51.41, 190.93) * mm});
            skLineSegment(sketch, "E660", {"start": v(-51.41, 429.32) * mm, "end": v(-0.27, 418) * mm});
            skLineSegment(sketch, "E661", {"start": v(-0.27, 418) * mm, "end": v(-0.27, 408.62) * mm});
            skLineSegment(sketch, "E662", {"start": v(-0.27, 408.62) * mm, "end": v(-51.24, 398.7) * mm});
            skLineSegment(sketch, "E663", {"start": v(-51.24, 398.7) * mm, "end": v(-51.41, 429.32) * mm});
            skLineSegment(sketch, "E664", {"start": v(-51.58, 651.97) * mm, "end": v(-0.24, 640.51) * mm});
            skLineSegment(sketch, "E665", {"start": v(-0.24, 640.51) * mm, "end": v(-0.24, 630.99) * mm});
            skLineSegment(sketch, "E666", {"start": v(-0.24, 630.99) * mm, "end": v(-51.58, 621.02) * mm});
            skLineSegment(sketch, "E667", {"start": v(-51.58, 621.02) * mm, "end": v(-51.58, 651.97) * mm});
            skLineSegment(sketch, "E668", {"start": v(-51.93, 869.16) * mm, "end": v(-0.38, 857.9) * mm});
            skLineSegment(sketch, "E669", {"start": v(-0.38, 857.9) * mm, "end": v(-0.38, 848.27) * mm});
            skLineSegment(sketch, "E670", {"start": v(-0.38, 848.27) * mm, "end": v(-51.68, 838.25) * mm});
            skLineSegment(sketch, "E671", {"start": v(-51.68, 838.25) * mm, "end": v(-51.93, 869.16) * mm});
            skLineSegment(sketch, "E672", {"start": v(-51.4, 1090.34) * mm, "end": v(-0.23, 1079.1) * mm});
            skLineSegment(sketch, "E673", {"start": v(-0.23, 1079.1) * mm, "end": v(-0.23, 1069.4) * mm});
            skLineSegment(sketch, "E674", {"start": v(-51.39, 1059.55) * mm, "end": v(-0.23, 1069.4) * mm});
            skLineSegment(sketch, "E675", {"start": v(-51.4, 1090.34) * mm, "end": v(-51.39, 1059.55) * mm});
            skLineSegment(sketch, "E676", {"start": v(308.37, 16.02) * mm, "end": v(359.79, 4.87) * mm});
            skLineSegment(sketch, "E677", {"start": v(359.79, 4.87) * mm, "end": v(359.79, -4.87) * mm});
            skLineSegment(sketch, "E678", {"start": v(359.79, -4.87) * mm, "end": v(308.37, -14.6) * mm});
            skLineSegment(sketch, "E679", {"start": v(308.37, -14.6) * mm, "end": v(308.37, 16.02) * mm});
            skLineSegment(sketch, "E680", {"start": v(308.37, -187.57) * mm, "end": v(359.6, -198.68) * mm});
            skLineSegment(sketch, "E681", {"start": v(359.6, -198.68) * mm, "end": v(359.6, -208.36) * mm});
            skLineSegment(sketch, "E682", {"start": v(359.6, -208.36) * mm, "end": v(308.37, -218.18) * mm});
            skLineSegment(sketch, "E683", {"start": v(308.37, -218.18) * mm, "end": v(308.37, -187.57) * mm});
            skLineSegment(sketch, "E684", {"start": v(308.33, -398.32) * mm, "end": v(359.54, -409.45) * mm});
            skLineSegment(sketch, "E685", {"start": v(359.54, -409.45) * mm, "end": v(359.54, -418.83) * mm});
            skLineSegment(sketch, "E686", {"start": v(359.54, -418.83) * mm, "end": v(308.11, -428.97) * mm});
            skLineSegment(sketch, "E687", {"start": v(308.11, -428.97) * mm, "end": v(308.33, -398.32) * mm});
            skLineSegment(sketch, "E688", {"start": v(308.37, 190.93) * mm, "end": v(359.68, 200.7) * mm});
            skLineSegment(sketch, "E689", {"start": v(359.68, 200.7) * mm, "end": v(359.68, 210.4) * mm});
            skLineSegment(sketch, "E690", {"start": v(359.68, 210.4) * mm, "end": v(308.3, 221.6) * mm});
            skLineSegment(sketch, "E691", {"start": v(308.3, 221.6) * mm, "end": v(308.37, 190.93) * mm});
            skLineSegment(sketch, "E692", {"start": v(308.37, 429.32) * mm, "end": v(359.51, 418) * mm});
            skLineSegment(sketch, "E693", {"start": v(359.51, 418) * mm, "end": v(359.51, 408.62) * mm});
            skLineSegment(sketch, "E694", {"start": v(359.51, 408.62) * mm, "end": v(308.55, 398.7) * mm});
            skLineSegment(sketch, "E695", {"start": v(308.55, 398.7) * mm, "end": v(308.37, 429.32) * mm});
            skLineSegment(sketch, "E696", {"start": v(308.2, 651.97) * mm, "end": v(359.54, 640.51) * mm});
            skLineSegment(sketch, "E697", {"start": v(359.54, 640.51) * mm, "end": v(359.54, 630.99) * mm});
            skLineSegment(sketch, "E698", {"start": v(359.54, 630.99) * mm, "end": v(308.2, 621.02) * mm});
            skLineSegment(sketch, "E699", {"start": v(308.2, 621.02) * mm, "end": v(308.2, 651.97) * mm});
            skLineSegment(sketch, "E700", {"start": v(307.85, 869.16) * mm, "end": v(359.4, 857.9) * mm});
            skLineSegment(sketch, "E701", {"start": v(359.4, 857.9) * mm, "end": v(359.4, 848.27) * mm});
            skLineSegment(sketch, "E702", {"start": v(359.4, 848.27) * mm, "end": v(308.1, 838.25) * mm});
            skLineSegment(sketch, "E703", {"start": v(308.1, 838.25) * mm, "end": v(307.85, 869.16) * mm});
            skLineSegment(sketch, "E704", {"start": v(308.39, 1090.34) * mm, "end": v(359.56, 1079.1) * mm});
            skLineSegment(sketch, "E705", {"start": v(359.56, 1079.1) * mm, "end": v(359.56, 1069.4) * mm});
            skLineSegment(sketch, "E706", {"start": v(308.4, 1059.55) * mm, "end": v(359.56, 1069.4) * mm});
            skLineSegment(sketch, "E707", {"start": v(308.39, 1090.34) * mm, "end": v(308.4, 1059.55) * mm});
            skLineSegment(sketch, "E708", {"start": v(694.77, 16.02) * mm, "end": v(746.18, 4.87) * mm});
            skLineSegment(sketch, "E709", {"start": v(746.18, 4.87) * mm, "end": v(746.18, -4.87) * mm});
            skLineSegment(sketch, "E710", {"start": v(746.18, -4.87) * mm, "end": v(694.77, -14.6) * mm});
            skLineSegment(sketch, "E711", {"start": v(694.77, -14.6) * mm, "end": v(694.77, 16.02) * mm});
            skLineSegment(sketch, "E712", {"start": v(694.77, -187.57) * mm, "end": v(746, -198.68) * mm});
            skLineSegment(sketch, "E713", {"start": v(746, -198.68) * mm, "end": v(746, -208.36) * mm});
            skLineSegment(sketch, "E714", {"start": v(746, -208.36) * mm, "end": v(694.77, -218.18) * mm});
            skLineSegment(sketch, "E715", {"start": v(694.77, -218.18) * mm, "end": v(694.77, -187.57) * mm});
            skLineSegment(sketch, "E716", {"start": v(694.72, -398.32) * mm, "end": v(745.94, -409.45) * mm});
            skLineSegment(sketch, "E717", {"start": v(745.94, -409.45) * mm, "end": v(745.94, -418.83) * mm});
            skLineSegment(sketch, "E718", {"start": v(745.94, -418.83) * mm, "end": v(694.5, -428.97) * mm});
            skLineSegment(sketch, "E719", {"start": v(694.5, -428.97) * mm, "end": v(694.72, -398.32) * mm});
            skLineSegment(sketch, "E720", {"start": v(694.77, 190.93) * mm, "end": v(746.07, 200.7) * mm});
            skLineSegment(sketch, "E721", {"start": v(746.07, 200.7) * mm, "end": v(746.07, 210.4) * mm});
            skLineSegment(sketch, "E722", {"start": v(746.07, 210.4) * mm, "end": v(694.7, 221.6) * mm});
            skLineSegment(sketch, "E723", {"start": v(694.7, 221.6) * mm, "end": v(694.77, 190.93) * mm});
            skLineSegment(sketch, "E724", {"start": v(694.77, 429.32) * mm, "end": v(745.9, 418) * mm});
            skLineSegment(sketch, "E725", {"start": v(745.9, 418) * mm, "end": v(745.9, 408.62) * mm});
            skLineSegment(sketch, "E726", {"start": v(745.9, 408.62) * mm, "end": v(694.94, 398.7) * mm});
            skLineSegment(sketch, "E727", {"start": v(694.94, 398.7) * mm, "end": v(694.77, 429.32) * mm});
            skLineSegment(sketch, "E728", {"start": v(694.6, 651.97) * mm, "end": v(745.94, 640.51) * mm});
            skLineSegment(sketch, "E729", {"start": v(745.94, 640.51) * mm, "end": v(745.94, 630.99) * mm});
            skLineSegment(sketch, "E730", {"start": v(745.94, 630.99) * mm, "end": v(694.6, 621.02) * mm});
            skLineSegment(sketch, "E731", {"start": v(694.6, 621.02) * mm, "end": v(694.6, 651.97) * mm});
            skLineSegment(sketch, "E732", {"start": v(694.25, 869.16) * mm, "end": v(745.8, 857.9) * mm});
            skLineSegment(sketch, "E733", {"start": v(745.8, 857.9) * mm, "end": v(745.8, 848.27) * mm});
            skLineSegment(sketch, "E734", {"start": v(745.8, 848.27) * mm, "end": v(694.5, 838.25) * mm});
            skLineSegment(sketch, "E735", {"start": v(694.5, 838.25) * mm, "end": v(694.25, 869.16) * mm});
            skLineSegment(sketch, "E736", {"start": v(694.78, 1090.34) * mm, "end": v(745.95, 1079.1) * mm});
            skLineSegment(sketch, "E737", {"start": v(745.95, 1079.1) * mm, "end": v(745.95, 1069.4) * mm});
            skLineSegment(sketch, "E738", {"start": v(694.8, 1059.55) * mm, "end": v(745.95, 1069.4) * mm});
            skLineSegment(sketch, "E739", {"start": v(694.78, 1090.34) * mm, "end": v(694.8, 1059.55) * mm});
            skLineSegment(sketch, "E740", {"start": v(1054.55, 16.02) * mm, "end": v(1105.97, 4.87) * mm});
            skLineSegment(sketch, "E741", {"start": v(1105.97, 4.87) * mm, "end": v(1105.97, -4.87) * mm});
            skLineSegment(sketch, "E742", {"start": v(1105.97, -4.87) * mm, "end": v(1054.55, -14.6) * mm});
            skLineSegment(sketch, "E743", {"start": v(1054.55, -14.6) * mm, "end": v(1054.55, 16.02) * mm});
            skLineSegment(sketch, "E744", {"start": v(1054.55, -187.57) * mm, "end": v(1105.78, -198.68) * mm});
            skLineSegment(sketch, "E745", {"start": v(1105.78, -198.68) * mm, "end": v(1105.78, -208.36) * mm});
            skLineSegment(sketch, "E746", {"start": v(1105.78, -208.36) * mm, "end": v(1054.55, -218.18) * mm});
            skLineSegment(sketch, "E747", {"start": v(1054.55, -218.18) * mm, "end": v(1054.55, -187.57) * mm});
            skLineSegment(sketch, "E748", {"start": v(1054.5, -398.32) * mm, "end": v(1105.72, -409.45) * mm});
            skLineSegment(sketch, "E749", {"start": v(1105.72, -409.45) * mm, "end": v(1105.72, -418.83) * mm});
            skLineSegment(sketch, "E750", {"start": v(1105.72, -418.83) * mm, "end": v(1054.3, -428.97) * mm});
            skLineSegment(sketch, "E751", {"start": v(1054.3, -428.97) * mm, "end": v(1054.5, -398.32) * mm});
            skLineSegment(sketch, "E752", {"start": v(1054.55, 190.93) * mm, "end": v(1105.86, 200.7) * mm});
            skLineSegment(sketch, "E753", {"start": v(1105.86, 200.7) * mm, "end": v(1105.86, 210.4) * mm});
            skLineSegment(sketch, "E754", {"start": v(1105.86, 210.4) * mm, "end": v(1054.5, 221.6) * mm});
            skLineSegment(sketch, "E755", {"start": v(1054.5, 221.6) * mm, "end": v(1054.55, 190.93) * mm});
            skLineSegment(sketch, "E756", {"start": v(1054.55, 429.32) * mm, "end": v(1105.7, 418) * mm});
            skLineSegment(sketch, "E757", {"start": v(1105.7, 418) * mm, "end": v(1105.7, 408.62) * mm});
            skLineSegment(sketch, "E758", {"start": v(1105.7, 408.62) * mm, "end": v(1054.73, 398.7) * mm});
            skLineSegment(sketch, "E759", {"start": v(1054.73, 398.7) * mm, "end": v(1054.55, 429.32) * mm});
            skLineSegment(sketch, "E760", {"start": v(1054.39, 651.97) * mm, "end": v(1105.73, 640.51) * mm});
            skLineSegment(sketch, "E761", {"start": v(1105.73, 640.51) * mm, "end": v(1105.73, 630.99) * mm});
            skLineSegment(sketch, "E762", {"start": v(1105.73, 630.99) * mm, "end": v(1054.39, 621.02) * mm});
            skLineSegment(sketch, "E763", {"start": v(1054.39, 621.02) * mm, "end": v(1054.39, 651.97) * mm});
            skLineSegment(sketch, "E764", {"start": v(1054.03, 869.16) * mm, "end": v(1105.59, 857.9) * mm});
            skLineSegment(sketch, "E765", {"start": v(1105.59, 857.9) * mm, "end": v(1105.59, 848.27) * mm});
            skLineSegment(sketch, "E766", {"start": v(1105.59, 848.27) * mm, "end": v(1054.28, 838.25) * mm});
            skLineSegment(sketch, "E767", {"start": v(1054.28, 838.25) * mm, "end": v(1054.03, 869.16) * mm});
            skLineSegment(sketch, "E768", {"start": v(1054.57, 1090.34) * mm, "end": v(1105.74, 1079.1) * mm});
            skLineSegment(sketch, "E769", {"start": v(1105.74, 1079.1) * mm, "end": v(1105.74, 1069.4) * mm});
            skLineSegment(sketch, "E770", {"start": v(1054.58, 1059.55) * mm, "end": v(1105.74, 1069.4) * mm});
            skLineSegment(sketch, "E771", {"start": v(1054.57, 1090.34) * mm, "end": v(1054.58, 1059.55) * mm});
            skLineSegment(sketch, "E772", {"start": v(1440.4, 15.8) * mm, "end": v(1491.82, 4.64) * mm});
            skLineSegment(sketch, "E773", {"start": v(1491.82, 4.64) * mm, "end": v(1491.82, -5.1) * mm});
            skLineSegment(sketch, "E774", {"start": v(1491.82, -5.1) * mm, "end": v(1440.4, -14.83) * mm});
            skLineSegment(sketch, "E775", {"start": v(1440.4, -14.83) * mm, "end": v(1440.4, 15.8) * mm});
            skLineSegment(sketch, "E776", {"start": v(1440.4, -187.79) * mm, "end": v(1491.63, -198.9) * mm});
            skLineSegment(sketch, "E777", {"start": v(1491.63, -198.9) * mm, "end": v(1491.63, -208.58) * mm});
            skLineSegment(sketch, "E778", {"start": v(1491.63, -208.58) * mm, "end": v(1440.4, -218.4) * mm});
            skLineSegment(sketch, "E779", {"start": v(1440.4, -218.4) * mm, "end": v(1440.4, -187.79) * mm});
            skLineSegment(sketch, "E780", {"start": v(1440.36, -398.55) * mm, "end": v(1491.57, -409.67) * mm});
            skLineSegment(sketch, "E781", {"start": v(1491.57, -409.67) * mm, "end": v(1491.57, -419.05) * mm});
            skLineSegment(sketch, "E782", {"start": v(1491.57, -419.05) * mm, "end": v(1440.14, -429.19) * mm});
            skLineSegment(sketch, "E783", {"start": v(1440.14, -429.19) * mm, "end": v(1440.36, -398.55) * mm});
            skLineSegment(sketch, "E784", {"start": v(1440.4, 190.71) * mm, "end": v(1491.7, 200.47) * mm});
            skLineSegment(sketch, "E785", {"start": v(1491.7, 200.47) * mm, "end": v(1491.7, 210.17) * mm});
            skLineSegment(sketch, "E786", {"start": v(1491.7, 210.17) * mm, "end": v(1440.34, 221.37) * mm});
            skLineSegment(sketch, "E787", {"start": v(1440.34, 221.37) * mm, "end": v(1440.4, 190.71) * mm});
            skLineSegment(sketch, "E788", {"start": v(1440.4, 429.1) * mm, "end": v(1491.55, 417.77) * mm});
            skLineSegment(sketch, "E789", {"start": v(1491.55, 417.77) * mm, "end": v(1491.55, 408.4) * mm});
            skLineSegment(sketch, "E790", {"start": v(1491.55, 408.4) * mm, "end": v(1440.58, 398.48) * mm});
            skLineSegment(sketch, "E791", {"start": v(1440.58, 398.48) * mm, "end": v(1440.4, 429.1) * mm});
            skLineSegment(sketch, "E792", {"start": v(1440.24, 651.75) * mm, "end": v(1491.58, 640.29) * mm});
            skLineSegment(sketch, "E793", {"start": v(1491.58, 640.29) * mm, "end": v(1491.58, 630.76) * mm});
            skLineSegment(sketch, "E794", {"start": v(1491.58, 630.76) * mm, "end": v(1440.24, 620.8) * mm});
            skLineSegment(sketch, "E795", {"start": v(1440.24, 620.8) * mm, "end": v(1440.24, 651.75) * mm});
            skLineSegment(sketch, "E796", {"start": v(1439.88, 868.94) * mm, "end": v(1491.44, 857.68) * mm});
            skLineSegment(sketch, "E797", {"start": v(1491.44, 857.68) * mm, "end": v(1491.44, 848.04) * mm});
            skLineSegment(sketch, "E798", {"start": v(1491.44, 848.04) * mm, "end": v(1440.13, 838.03) * mm});
            skLineSegment(sketch, "E799", {"start": v(1440.13, 838.03) * mm, "end": v(1439.88, 868.94) * mm});
            skLineSegment(sketch, "E800", {"start": v(1440.42, 1090.12) * mm, "end": v(1491.6, 1078.88) * mm});
            skLineSegment(sketch, "E801", {"start": v(1491.6, 1078.88) * mm, "end": v(1491.6, 1069.18) * mm});
            skLineSegment(sketch, "E802", {"start": v(1440.43, 1059.32) * mm, "end": v(1491.6, 1069.18) * mm});
            skLineSegment(sketch, "E803", {"start": v(1440.42, 1090.12) * mm, "end": v(1440.43, 1059.32) * mm});
            skLineSegment(sketch, "E804", {"start": v(1800.19, 15.8) * mm, "end": v(1851.6, 4.64) * mm});
            skLineSegment(sketch, "E805", {"start": v(1851.6, 4.64) * mm, "end": v(1851.6, -5.1) * mm});
            skLineSegment(sketch, "E806", {"start": v(1851.6, -5.1) * mm, "end": v(1800.19, -14.83) * mm});
            skLineSegment(sketch, "E807", {"start": v(1800.19, -14.83) * mm, "end": v(1800.19, 15.8) * mm});
            skLineSegment(sketch, "E808", {"start": v(1800.19, -187.79) * mm, "end": v(1851.42, -198.9) * mm});
            skLineSegment(sketch, "E809", {"start": v(1851.42, -198.9) * mm, "end": v(1851.42, -208.58) * mm});
            skLineSegment(sketch, "E810", {"start": v(1851.42, -208.58) * mm, "end": v(1800.19, -218.4) * mm});
            skLineSegment(sketch, "E811", {"start": v(1800.19, -218.4) * mm, "end": v(1800.19, -187.79) * mm});
            skLineSegment(sketch, "E812", {"start": v(1800.14, -398.55) * mm, "end": v(1851.36, -409.67) * mm});
            skLineSegment(sketch, "E813", {"start": v(1851.36, -409.67) * mm, "end": v(1851.36, -419.05) * mm});
            skLineSegment(sketch, "E814", {"start": v(1851.36, -419.05) * mm, "end": v(1799.93, -429.19) * mm});
            skLineSegment(sketch, "E815", {"start": v(1799.93, -429.19) * mm, "end": v(1800.14, -398.55) * mm});
            skLineSegment(sketch, "E816", {"start": v(1800.19, 190.71) * mm, "end": v(1851.5, 200.47) * mm});
            skLineSegment(sketch, "E817", {"start": v(1851.5, 200.47) * mm, "end": v(1851.5, 210.17) * mm});
            skLineSegment(sketch, "E818", {"start": v(1851.5, 210.17) * mm, "end": v(1800.13, 221.37) * mm});
            skLineSegment(sketch, "E819", {"start": v(1800.13, 221.37) * mm, "end": v(1800.19, 190.71) * mm});
            skLineSegment(sketch, "E820", {"start": v(1800.19, 429.1) * mm, "end": v(1851.33, 417.77) * mm});
            skLineSegment(sketch, "E821", {"start": v(1851.33, 417.77) * mm, "end": v(1851.33, 408.4) * mm});
            skLineSegment(sketch, "E822", {"start": v(1851.33, 408.4) * mm, "end": v(1800.37, 398.48) * mm});
            skLineSegment(sketch, "E823", {"start": v(1800.37, 398.48) * mm, "end": v(1800.19, 429.1) * mm});
            skLineSegment(sketch, "E824", {"start": v(1800.02, 651.75) * mm, "end": v(1851.36, 640.29) * mm});
            skLineSegment(sketch, "E825", {"start": v(1851.36, 640.29) * mm, "end": v(1851.36, 630.76) * mm});
            skLineSegment(sketch, "E826", {"start": v(1851.36, 630.76) * mm, "end": v(1800.02, 620.8) * mm});
            skLineSegment(sketch, "E827", {"start": v(1800.02, 620.8) * mm, "end": v(1800.02, 651.75) * mm});
            skLineSegment(sketch, "E828", {"start": v(1799.67, 868.94) * mm, "end": v(1851.22, 857.68) * mm});
            skLineSegment(sketch, "E829", {"start": v(1851.22, 857.68) * mm, "end": v(1851.22, 848.04) * mm});
            skLineSegment(sketch, "E830", {"start": v(1851.22, 848.04) * mm, "end": v(1799.92, 838.03) * mm});
            skLineSegment(sketch, "E831", {"start": v(1799.92, 838.03) * mm, "end": v(1799.67, 868.94) * mm});
            skLineSegment(sketch, "E832", {"start": v(1800.2, 1090.12) * mm, "end": v(1851.38, 1078.88) * mm});
            skLineSegment(sketch, "E833", {"start": v(1851.38, 1078.88) * mm, "end": v(1851.38, 1069.18) * mm});
            skLineSegment(sketch, "E834", {"start": v(1800.21, 1059.32) * mm, "end": v(1851.38, 1069.18) * mm});
            skLineSegment(sketch, "E835", {"start": v(1800.2, 1090.12) * mm, "end": v(1800.21, 1059.32) * mm});
            skLineSegment(sketch, "E836", {"start": v(2186.58, 15.8) * mm, "end": v(2238, 4.64) * mm});
            skLineSegment(sketch, "E837", {"start": v(2238, 4.64) * mm, "end": v(2238, -5.1) * mm});
            skLineSegment(sketch, "E838", {"start": v(2238, -5.1) * mm, "end": v(2186.58, -14.83) * mm});
            skLineSegment(sketch, "E839", {"start": v(2186.58, -14.83) * mm, "end": v(2186.58, 15.8) * mm});
            skLineSegment(sketch, "E840", {"start": v(2186.58, -187.79) * mm, "end": v(2237.81, -198.9) * mm});
            skLineSegment(sketch, "E841", {"start": v(2237.81, -198.9) * mm, "end": v(2237.81, -208.58) * mm});
            skLineSegment(sketch, "E842", {"start": v(2237.81, -208.58) * mm, "end": v(2186.58, -218.4) * mm});
            skLineSegment(sketch, "E843", {"start": v(2186.58, -218.4) * mm, "end": v(2186.58, -187.79) * mm});
            skLineSegment(sketch, "E844", {"start": v(2186.54, -398.55) * mm, "end": v(2237.76, -409.67) * mm});
            skLineSegment(sketch, "E845", {"start": v(2237.76, -409.67) * mm, "end": v(2237.76, -419.05) * mm});
            skLineSegment(sketch, "E846", {"start": v(2237.76, -419.05) * mm, "end": v(2186.33, -429.19) * mm});
            skLineSegment(sketch, "E847", {"start": v(2186.33, -429.19) * mm, "end": v(2186.54, -398.55) * mm});
            skLineSegment(sketch, "E848", {"start": v(2186.58, 190.71) * mm, "end": v(2237.89, 200.47) * mm});
            skLineSegment(sketch, "E849", {"start": v(2237.89, 200.47) * mm, "end": v(2237.89, 210.17) * mm});
            skLineSegment(sketch, "E850", {"start": v(2237.89, 210.17) * mm, "end": v(2186.52, 221.37) * mm});
            skLineSegment(sketch, "E851", {"start": v(2186.52, 221.37) * mm, "end": v(2186.58, 190.71) * mm});
            skLineSegment(sketch, "E852", {"start": v(2186.58, 429.1) * mm, "end": v(2237.73, 417.77) * mm});
            skLineSegment(sketch, "E853", {"start": v(2237.73, 417.77) * mm, "end": v(2237.73, 408.4) * mm});
            skLineSegment(sketch, "E854", {"start": v(2237.73, 408.4) * mm, "end": v(2186.76, 398.48) * mm});
            skLineSegment(sketch, "E855", {"start": v(2186.76, 398.48) * mm, "end": v(2186.58, 429.1) * mm});
            skLineSegment(sketch, "E856", {"start": v(2186.42, 651.75) * mm, "end": v(2237.76, 640.29) * mm});
            skLineSegment(sketch, "E857", {"start": v(2237.76, 640.29) * mm, "end": v(2237.76, 630.76) * mm});
            skLineSegment(sketch, "E858", {"start": v(2237.76, 630.76) * mm, "end": v(2186.42, 620.8) * mm});
            skLineSegment(sketch, "E859", {"start": v(2186.42, 620.8) * mm, "end": v(2186.42, 651.75) * mm});
            skLineSegment(sketch, "E860", {"start": v(2186.06, 868.94) * mm, "end": v(2237.62, 857.68) * mm});
            skLineSegment(sketch, "E861", {"start": v(2237.62, 857.68) * mm, "end": v(2237.62, 848.04) * mm});
            skLineSegment(sketch, "E862", {"start": v(2237.62, 848.04) * mm, "end": v(2186.31, 838.03) * mm});
            skLineSegment(sketch, "E863", {"start": v(2186.31, 838.03) * mm, "end": v(2186.06, 868.94) * mm});
            skLineSegment(sketch, "E864", {"start": v(2186.6, 1090.12) * mm, "end": v(2237.77, 1078.88) * mm});
            skLineSegment(sketch, "E865", {"start": v(2237.77, 1078.88) * mm, "end": v(2237.77, 1069.18) * mm});
            skLineSegment(sketch, "E866", {"start": v(2186.6, 1059.32) * mm, "end": v(2237.77, 1069.18) * mm});
            skLineSegment(sketch, "E867", {"start": v(2186.6, 1090.12) * mm, "end": v(2186.6, 1059.32) * mm});
            skLineSegment(sketch, "E868", {"start": v(2546.37, 15.8) * mm, "end": v(2597.78, 4.64) * mm});
            skLineSegment(sketch, "E869", {"start": v(2597.78, 4.64) * mm, "end": v(2597.78, -5.1) * mm});
            skLineSegment(sketch, "E870", {"start": v(2597.78, -5.1) * mm, "end": v(2546.37, -14.83) * mm});
            skLineSegment(sketch, "E871", {"start": v(2546.37, -14.83) * mm, "end": v(2546.37, 15.8) * mm});
            skLineSegment(sketch, "E872", {"start": v(2546.37, -187.79) * mm, "end": v(2597.6, -198.9) * mm});
            skLineSegment(sketch, "E873", {"start": v(2597.6, -198.9) * mm, "end": v(2597.6, -208.58) * mm});
            skLineSegment(sketch, "E874", {"start": v(2597.6, -208.58) * mm, "end": v(2546.37, -218.4) * mm});
            skLineSegment(sketch, "E875", {"start": v(2546.37, -218.4) * mm, "end": v(2546.37, -187.79) * mm});
            skLineSegment(sketch, "E876", {"start": v(2546.32, -398.55) * mm, "end": v(2597.54, -409.67) * mm});
            skLineSegment(sketch, "E877", {"start": v(2597.54, -409.67) * mm, "end": v(2597.54, -419.05) * mm});
            skLineSegment(sketch, "E878", {"start": v(2597.54, -419.05) * mm, "end": v(2546.11, -429.19) * mm});
            skLineSegment(sketch, "E879", {"start": v(2546.11, -429.19) * mm, "end": v(2546.32, -398.55) * mm});
            skLineSegment(sketch, "E880", {"start": v(2546.37, 190.71) * mm, "end": v(2597.68, 200.47) * mm});
            skLineSegment(sketch, "E881", {"start": v(2597.68, 200.47) * mm, "end": v(2597.68, 210.17) * mm});
            skLineSegment(sketch, "E882", {"start": v(2597.68, 210.17) * mm, "end": v(2546.3, 221.37) * mm});
            skLineSegment(sketch, "E883", {"start": v(2546.3, 221.37) * mm, "end": v(2546.37, 190.71) * mm});
            skLineSegment(sketch, "E884", {"start": v(2546.37, 429.1) * mm, "end": v(2597.51, 417.77) * mm});
            skLineSegment(sketch, "E885", {"start": v(2597.51, 417.77) * mm, "end": v(2597.51, 408.4) * mm});
            skLineSegment(sketch, "E886", {"start": v(2597.51, 408.4) * mm, "end": v(2546.55, 398.48) * mm});
            skLineSegment(sketch, "E887", {"start": v(2546.55, 398.48) * mm, "end": v(2546.37, 429.1) * mm});
            skLineSegment(sketch, "E888", {"start": v(2546.2, 651.75) * mm, "end": v(2597.54, 640.29) * mm});
            skLineSegment(sketch, "E889", {"start": v(2597.54, 640.29) * mm, "end": v(2597.54, 630.76) * mm});
            skLineSegment(sketch, "E890", {"start": v(2597.54, 630.76) * mm, "end": v(2546.2, 620.8) * mm});
            skLineSegment(sketch, "E891", {"start": v(2546.2, 620.8) * mm, "end": v(2546.2, 651.75) * mm});
            skLineSegment(sketch, "E892", {"start": v(2545.85, 868.94) * mm, "end": v(2597.4, 857.68) * mm});
            skLineSegment(sketch, "E893", {"start": v(2597.4, 857.68) * mm, "end": v(2597.4, 848.04) * mm});
            skLineSegment(sketch, "E894", {"start": v(2597.4, 848.04) * mm, "end": v(2546.1, 838.03) * mm});
            skLineSegment(sketch, "E895", {"start": v(2546.1, 838.03) * mm, "end": v(2545.85, 868.94) * mm});
            skLineSegment(sketch, "E896", {"start": v(2546.39, 1090.12) * mm, "end": v(2597.56, 1078.88) * mm});
            skLineSegment(sketch, "E897", {"start": v(2597.56, 1078.88) * mm, "end": v(2597.56, 1069.18) * mm});
            skLineSegment(sketch, "E898", {"start": v(2546.4, 1059.32) * mm, "end": v(2597.56, 1069.18) * mm});
            skLineSegment(sketch, "E899", {"start": v(2546.39, 1090.12) * mm, "end": v(2546.4, 1059.32) * mm});
            skSolve(sketch);
        }
        {
            var Q0;
            Q0=qSketchRegion(id+"F4",true);
            extrude(context, id + "F5", {"entities" : qUnion([Q0]), "depth" : 7.62 * mm, "offsetDistance" : 25.4 * mm});
        }
        {
            var Q0;
            Q0=makeQuery(id+"F5.opExtrude","CAP_FACE",FACE,{"disambiguationData":[OSD([sQuery(id+"F4.wireOp",EDGE,"E644"),sQuery(id+"F4.wireOp",EDGE,"E645"),sQuery(id+"F4.wireOp",EDGE,"E646"),sQuery(id+"F4.wireOp",EDGE,"E647")])],"isStart":false});
            var sketch = newSketch(context, id + "F6", { "sketchPlane" : qUnion([Q0])});
            skLineSegment(sketch, "E900", {"start": v(-51.41, 16.02) * mm, "end": v(0, 4.87) * mm});
            skLineSegment(sketch, "E901", {"start": v(0, 4.87) * mm, "end": v(0, -4.87) * mm});
            skLineSegment(sketch, "E902", {"start": v(0, -4.87) * mm, "end": v(-51.41, -14.6) * mm});
            skLineSegment(sketch, "E903", {"start": v(-51.41, -14.6) * mm, "end": v(-51.41, 16.02) * mm});
            skLineSegment(sketch, "E904", {"start": v(-51.52, -398.25) * mm, "end": v(-51.52, -428.6) * mm});
            skLineSegment(sketch, "E905", {"start": v(-51.52, -398.25) * mm, "end": v(-0.18, -409.56) * mm});
            skLineSegment(sketch, "E906", {"start": v(-0.18, -409.56) * mm, "end": v(-0.18, -418.79) * mm});
            skLineSegment(sketch, "E907", {"start": v(-0.18, -418.79) * mm, "end": v(-51.52, -428.6) * mm});
            skLineSegment(sketch, "E908", {"start": v(-51.34, -187.52) * mm, "end": v(-0.23, -198.69) * mm});
            skLineSegment(sketch, "E909", {"start": v(-0.23, -198.69) * mm, "end": v(-0.23, -208.28) * mm});
            skLineSegment(sketch, "E910", {"start": v(-0.23, -208.28) * mm, "end": v(-51.42, -218.1) * mm});
            skLineSegment(sketch, "E911", {"start": v(-51.42, -218.1) * mm, "end": v(-51.34, -187.52) * mm});
            skLineSegment(sketch, "E912", {"start": v(-51.38, 221.63) * mm, "end": v(-0.12, 210.32) * mm});
            skLineSegment(sketch, "E913", {"start": v(-0.12, 210.32) * mm, "end": v(-0.12, 200.72) * mm});
            skLineSegment(sketch, "E914", {"start": v(-0.12, 200.72) * mm, "end": v(-51.46, 190.9) * mm});
            skLineSegment(sketch, "E915", {"start": v(-51.46, 190.9) * mm, "end": v(-51.38, 221.63) * mm});
            skLineSegment(sketch, "E916", {"start": v(-51.23, 429.4) * mm, "end": v(-0.26, 417.82) * mm});
            skLineSegment(sketch, "E917", {"start": v(-0.26, 417.82) * mm, "end": v(-0.26, 408.52) * mm});
            skLineSegment(sketch, "E918", {"start": v(-0.26, 408.52) * mm, "end": v(-51.23, 398.8) * mm});
            skLineSegment(sketch, "E919", {"start": v(-51.23, 398.8) * mm, "end": v(-51.23, 429.4) * mm});
            skLineSegment(sketch, "E920", {"start": v(-51.43, 651.93) * mm, "end": v(-0.16, 640.4) * mm});
            skLineSegment(sketch, "E921", {"start": v(-0.16, 640.4) * mm, "end": v(-0.16, 631.17) * mm});
            skLineSegment(sketch, "E922", {"start": v(-0.16, 631.17) * mm, "end": v(-51.43, 621.2) * mm});
            skLineSegment(sketch, "E923", {"start": v(-51.72, 869.28) * mm, "end": v(-0.05, 857.77) * mm});
            skLineSegment(sketch, "E924", {"start": v(-0.05, 857.77) * mm, "end": v(-0.05, 848.48) * mm});
            skLineSegment(sketch, "E925", {"start": v(-0.05, 848.48) * mm, "end": v(-51.72, 838.3) * mm});
            skLineSegment(sketch, "E926", {"start": v(-51.72, 838.3) * mm, "end": v(-51.72, 869.28) * mm});
            skLineSegment(sketch, "E927", {"start": v(-51.22, 1090.31) * mm, "end": v(-0.1, 1078.92) * mm});
            skLineSegment(sketch, "E928", {"start": v(-0.1, 1078.92) * mm, "end": v(-0.1, 1069.6) * mm});
            skLineSegment(sketch, "E929", {"start": v(-0.1, 1069.6) * mm, "end": v(-51.22, 1059.65) * mm});
            skLineSegment(sketch, "E930", {"start": v(-51.22, 1059.65) * mm, "end": v(-51.22, 1090.31) * mm});
            skLineSegment(sketch, "E931", {"start": v(-51.43, 651.93) * mm, "end": v(-51.43, 621.2) * mm});
            skLineSegment(sketch, "E932", {"start": v(308.65, 16.02) * mm, "end": v(360.06, 4.87) * mm});
            skLineSegment(sketch, "E933", {"start": v(360.06, 4.87) * mm, "end": v(360.06, -4.87) * mm});
            skLineSegment(sketch, "E934", {"start": v(360.06, -4.87) * mm, "end": v(308.65, -14.6) * mm});
            skLineSegment(sketch, "E935", {"start": v(308.65, -14.6) * mm, "end": v(308.65, 16.02) * mm});
            skLineSegment(sketch, "E936", {"start": v(308.55, -398.25) * mm, "end": v(308.55, -428.6) * mm});
            skLineSegment(sketch, "E937", {"start": v(308.55, -398.25) * mm, "end": v(359.89, -409.56) * mm});
            skLineSegment(sketch, "E938", {"start": v(359.89, -409.56) * mm, "end": v(359.89, -418.79) * mm});
            skLineSegment(sketch, "E939", {"start": v(359.89, -418.79) * mm, "end": v(308.55, -428.6) * mm});
            skLineSegment(sketch, "E940", {"start": v(308.72, -187.52) * mm, "end": v(359.84, -198.69) * mm});
            skLineSegment(sketch, "E941", {"start": v(359.84, -198.69) * mm, "end": v(359.84, -208.28) * mm});
            skLineSegment(sketch, "E942", {"start": v(359.84, -208.28) * mm, "end": v(308.65, -218.1) * mm});
            skLineSegment(sketch, "E943", {"start": v(308.65, -218.1) * mm, "end": v(308.72, -187.52) * mm});
            skLineSegment(sketch, "E944", {"start": v(308.68, 221.63) * mm, "end": v(359.94, 210.32) * mm});
            skLineSegment(sketch, "E945", {"start": v(359.94, 210.32) * mm, "end": v(359.94, 200.72) * mm});
            skLineSegment(sketch, "E946", {"start": v(359.94, 200.72) * mm, "end": v(308.6, 190.9) * mm});
            skLineSegment(sketch, "E947", {"start": v(308.6, 190.9) * mm, "end": v(308.68, 221.63) * mm});
            skLineSegment(sketch, "E948", {"start": v(308.83, 429.4) * mm, "end": v(359.8, 417.82) * mm});
            skLineSegment(sketch, "E949", {"start": v(359.8, 417.82) * mm, "end": v(359.8, 408.52) * mm});
            skLineSegment(sketch, "E950", {"start": v(359.8, 408.52) * mm, "end": v(308.83, 398.8) * mm});
            skLineSegment(sketch, "E951", {"start": v(308.83, 398.8) * mm, "end": v(308.83, 429.4) * mm});
            skLineSegment(sketch, "E952", {"start": v(308.63, 651.93) * mm, "end": v(359.9, 640.4) * mm});
            skLineSegment(sketch, "E953", {"start": v(359.9, 640.4) * mm, "end": v(359.9, 631.17) * mm});
            skLineSegment(sketch, "E954", {"start": v(359.9, 631.17) * mm, "end": v(308.63, 621.2) * mm});
            skLineSegment(sketch, "E955", {"start": v(308.34, 869.28) * mm, "end": v(360.02, 857.77) * mm});
            skLineSegment(sketch, "E956", {"start": v(360.02, 857.77) * mm, "end": v(360.02, 848.48) * mm});
            skLineSegment(sketch, "E957", {"start": v(360.02, 848.48) * mm, "end": v(308.34, 838.3) * mm});
            skLineSegment(sketch, "E958", {"start": v(308.34, 838.3) * mm, "end": v(308.34, 869.28) * mm});
            skLineSegment(sketch, "E959", {"start": v(308.85, 1090.31) * mm, "end": v(359.96, 1078.92) * mm});
            skLineSegment(sketch, "E960", {"start": v(359.96, 1078.92) * mm, "end": v(359.96, 1069.6) * mm});
            skLineSegment(sketch, "E961", {"start": v(359.96, 1069.6) * mm, "end": v(308.85, 1059.65) * mm});
            skLineSegment(sketch, "E962", {"start": v(308.85, 1059.65) * mm, "end": v(308.85, 1090.31) * mm});
            skLineSegment(sketch, "E963", {"start": v(308.63, 651.93) * mm, "end": v(308.63, 621.2) * mm});
            skLineSegment(sketch, "E964", {"start": v(694.53, 15.77) * mm, "end": v(745.94, 4.62) * mm});
            skLineSegment(sketch, "E965", {"start": v(745.94, 4.62) * mm, "end": v(745.94, -5.12) * mm});
            skLineSegment(sketch, "E966", {"start": v(745.94, -5.12) * mm, "end": v(694.53, -14.85) * mm});
            skLineSegment(sketch, "E967", {"start": v(694.53, -14.85) * mm, "end": v(694.53, 15.77) * mm});
            skLineSegment(sketch, "E968", {"start": v(694.43, -398.5) * mm, "end": v(694.43, -428.86) * mm});
            skLineSegment(sketch, "E969", {"start": v(694.43, -398.5) * mm, "end": v(745.76, -409.81) * mm});
            skLineSegment(sketch, "E970", {"start": v(745.76, -409.81) * mm, "end": v(745.76, -419.04) * mm});
            skLineSegment(sketch, "E971", {"start": v(745.76, -419.04) * mm, "end": v(694.43, -428.86) * mm});
            skLineSegment(sketch, "E972", {"start": v(694.6, -187.78) * mm, "end": v(745.72, -198.94) * mm});
            skLineSegment(sketch, "E973", {"start": v(745.72, -198.94) * mm, "end": v(745.72, -208.53) * mm});
            skLineSegment(sketch, "E974", {"start": v(745.72, -208.53) * mm, "end": v(694.52, -218.36) * mm});
            skLineSegment(sketch, "E975", {"start": v(694.52, -218.36) * mm, "end": v(694.6, -187.78) * mm});
            skLineSegment(sketch, "E976", {"start": v(694.56, 221.38) * mm, "end": v(745.82, 210.07) * mm});
            skLineSegment(sketch, "E977", {"start": v(745.82, 210.07) * mm, "end": v(745.82, 200.47) * mm});
            skLineSegment(sketch, "E978", {"start": v(745.82, 200.47) * mm, "end": v(694.48, 190.65) * mm});
            skLineSegment(sketch, "E979", {"start": v(694.48, 190.65) * mm, "end": v(694.56, 221.38) * mm});
            skLineSegment(sketch, "E980", {"start": v(694.71, 429.16) * mm, "end": v(745.68, 417.56) * mm});
            skLineSegment(sketch, "E981", {"start": v(745.68, 417.56) * mm, "end": v(745.68, 408.27) * mm});
            skLineSegment(sketch, "E982", {"start": v(745.68, 408.27) * mm, "end": v(694.71, 398.54) * mm});
            skLineSegment(sketch, "E983", {"start": v(694.71, 398.54) * mm, "end": v(694.71, 429.16) * mm});
            skLineSegment(sketch, "E984", {"start": v(694.51, 651.68) * mm, "end": v(745.78, 640.14) * mm});
            skLineSegment(sketch, "E985", {"start": v(745.78, 640.14) * mm, "end": v(745.78, 630.92) * mm});
            skLineSegment(sketch, "E986", {"start": v(745.78, 630.92) * mm, "end": v(694.51, 620.95) * mm});
            skLineSegment(sketch, "E987", {"start": v(694.22, 869.02) * mm, "end": v(745.9, 857.52) * mm});
            skLineSegment(sketch, "E988", {"start": v(745.9, 857.52) * mm, "end": v(745.9, 848.23) * mm});
            skLineSegment(sketch, "E989", {"start": v(745.9, 848.23) * mm, "end": v(694.22, 838.06) * mm});
            skLineSegment(sketch, "E990", {"start": v(694.22, 838.06) * mm, "end": v(694.22, 869.02) * mm});
            skLineSegment(sketch, "E991", {"start": v(694.73, 1090.06) * mm, "end": v(745.84, 1078.67) * mm});
            skLineSegment(sketch, "E992", {"start": v(745.84, 1078.67) * mm, "end": v(745.84, 1069.35) * mm});
            skLineSegment(sketch, "E993", {"start": v(745.84, 1069.35) * mm, "end": v(694.73, 1059.4) * mm});
            skLineSegment(sketch, "E994", {"start": v(694.73, 1059.4) * mm, "end": v(694.73, 1090.06) * mm});
            skLineSegment(sketch, "E995", {"start": v(694.51, 651.68) * mm, "end": v(694.51, 620.95) * mm});
            skLineSegment(sketch, "E996", {"start": v(1054.59, 15.77) * mm, "end": v(1106, 4.62) * mm});
            skLineSegment(sketch, "E997", {"start": v(1106, 4.62) * mm, "end": v(1106, -5.12) * mm});
            skLineSegment(sketch, "E998", {"start": v(1106, -5.12) * mm, "end": v(1054.59, -14.85) * mm});
            skLineSegment(sketch, "E999", {"start": v(1054.59, -14.85) * mm, "end": v(1054.59, 15.77) * mm});
            skLineSegment(sketch, "E1000", {"start": v(1054.49, -398.5) * mm, "end": v(1054.49, -428.86) * mm});
            skLineSegment(sketch, "E1001", {"start": v(1054.49, -398.5) * mm, "end": v(1105.83, -409.81) * mm});
            skLineSegment(sketch, "E1002", {"start": v(1105.83, -409.81) * mm, "end": v(1105.83, -419.04) * mm});
            skLineSegment(sketch, "E1003", {"start": v(1105.83, -419.04) * mm, "end": v(1054.49, -428.86) * mm});
            skLineSegment(sketch, "E1004", {"start": v(1054.66, -187.78) * mm, "end": v(1105.78, -198.94) * mm});
            skLineSegment(sketch, "E1005", {"start": v(1105.78, -198.94) * mm, "end": v(1105.78, -208.53) * mm});
            skLineSegment(sketch, "E1006", {"start": v(1105.78, -208.53) * mm, "end": v(1054.59, -218.36) * mm});
            skLineSegment(sketch, "E1007", {"start": v(1054.59, -218.36) * mm, "end": v(1054.66, -187.78) * mm});
            skLineSegment(sketch, "E1008", {"start": v(1054.62, 221.38) * mm, "end": v(1105.88, 210.07) * mm});
            skLineSegment(sketch, "E1009", {"start": v(1105.88, 210.07) * mm, "end": v(1105.88, 200.47) * mm});
            skLineSegment(sketch, "E1010", {"start": v(1105.88, 200.47) * mm, "end": v(1054.54, 190.65) * mm});
            skLineSegment(sketch, "E1011", {"start": v(1054.54, 190.65) * mm, "end": v(1054.62, 221.38) * mm});
            skLineSegment(sketch, "E1012", {"start": v(1054.77, 429.16) * mm, "end": v(1105.74, 417.56) * mm});
            skLineSegment(sketch, "E1013", {"start": v(1105.74, 417.56) * mm, "end": v(1105.74, 408.27) * mm});
            skLineSegment(sketch, "E1014", {"start": v(1105.74, 408.27) * mm, "end": v(1054.77, 398.54) * mm});
            skLineSegment(sketch, "E1015", {"start": v(1054.77, 398.54) * mm, "end": v(1054.77, 429.16) * mm});
            skLineSegment(sketch, "E1016", {"start": v(1054.58, 651.68) * mm, "end": v(1105.84, 640.14) * mm});
            skLineSegment(sketch, "E1017", {"start": v(1105.84, 640.14) * mm, "end": v(1105.84, 630.92) * mm});
            skLineSegment(sketch, "E1018", {"start": v(1105.84, 630.92) * mm, "end": v(1054.58, 620.95) * mm});
            skLineSegment(sketch, "E1019", {"start": v(1054.28, 869.02) * mm, "end": v(1105.96, 857.52) * mm});
            skLineSegment(sketch, "E1020", {"start": v(1105.96, 857.52) * mm, "end": v(1105.96, 848.23) * mm});
            skLineSegment(sketch, "E1021", {"start": v(1105.96, 848.23) * mm, "end": v(1054.28, 838.06) * mm});
            skLineSegment(sketch, "E1022", {"start": v(1054.28, 838.06) * mm, "end": v(1054.28, 869.02) * mm});
            skLineSegment(sketch, "E1023", {"start": v(1054.79, 1090.06) * mm, "end": v(1105.9, 1078.67) * mm});
            skLineSegment(sketch, "E1024", {"start": v(1105.9, 1078.67) * mm, "end": v(1105.9, 1069.35) * mm});
            skLineSegment(sketch, "E1025", {"start": v(1105.9, 1069.35) * mm, "end": v(1054.79, 1059.4) * mm});
            skLineSegment(sketch, "E1026", {"start": v(1054.79, 1059.4) * mm, "end": v(1054.79, 1090.06) * mm});
            skLineSegment(sketch, "E1027", {"start": v(1054.58, 651.68) * mm, "end": v(1054.58, 620.95) * mm});
            skLineSegment(sketch, "E1028", {"start": v(1440.26, 15.94) * mm, "end": v(1491.67, 4.79) * mm});
            skLineSegment(sketch, "E1029", {"start": v(1491.67, 4.79) * mm, "end": v(1491.67, -4.95) * mm});
            skLineSegment(sketch, "E1030", {"start": v(1491.67, -4.95) * mm, "end": v(1440.26, -14.69) * mm});
            skLineSegment(sketch, "E1031", {"start": v(1440.26, -14.69) * mm, "end": v(1440.26, 15.94) * mm});
            skLineSegment(sketch, "E1032", {"start": v(1440.16, -398.33) * mm, "end": v(1440.16, -428.69) * mm});
            skLineSegment(sketch, "E1033", {"start": v(1440.16, -398.33) * mm, "end": v(1491.5, -409.64) * mm});
            skLineSegment(sketch, "E1034", {"start": v(1491.5, -409.64) * mm, "end": v(1491.5, -418.87) * mm});
            skLineSegment(sketch, "E1035", {"start": v(1491.5, -418.87) * mm, "end": v(1440.16, -428.69) * mm});
            skLineSegment(sketch, "E1036", {"start": v(1440.33, -187.6) * mm, "end": v(1491.45, -198.77) * mm});
            skLineSegment(sketch, "E1037", {"start": v(1491.45, -198.77) * mm, "end": v(1491.45, -208.37) * mm});
            skLineSegment(sketch, "E1038", {"start": v(1491.45, -208.37) * mm, "end": v(1440.26, -218.19) * mm});
            skLineSegment(sketch, "E1039", {"start": v(1440.26, -218.19) * mm, "end": v(1440.33, -187.6) * mm});
            skLineSegment(sketch, "E1040", {"start": v(1440.3, 221.55) * mm, "end": v(1491.56, 210.24) * mm});
            skLineSegment(sketch, "E1041", {"start": v(1491.56, 210.24) * mm, "end": v(1491.56, 200.64) * mm});
            skLineSegment(sketch, "E1042", {"start": v(1491.56, 200.64) * mm, "end": v(1440.22, 190.82) * mm});
            skLineSegment(sketch, "E1043", {"start": v(1440.22, 190.82) * mm, "end": v(1440.3, 221.55) * mm});
            skLineSegment(sketch, "E1044", {"start": v(1440.45, 429.32) * mm, "end": v(1491.41, 417.73) * mm});
            skLineSegment(sketch, "E1045", {"start": v(1491.41, 417.73) * mm, "end": v(1491.41, 408.44) * mm});
            skLineSegment(sketch, "E1046", {"start": v(1491.41, 408.44) * mm, "end": v(1440.45, 398.7) * mm});
            skLineSegment(sketch, "E1047", {"start": v(1440.45, 398.7) * mm, "end": v(1440.45, 429.32) * mm});
            skLineSegment(sketch, "E1048", {"start": v(1440.25, 651.84) * mm, "end": v(1491.51, 640.31) * mm});
            skLineSegment(sketch, "E1049", {"start": v(1491.51, 640.31) * mm, "end": v(1491.51, 631.09) * mm});
            skLineSegment(sketch, "E1050", {"start": v(1491.51, 631.09) * mm, "end": v(1440.25, 621.12) * mm});
            skLineSegment(sketch, "E1051", {"start": v(1439.95, 869.2) * mm, "end": v(1491.63, 857.7) * mm});
            skLineSegment(sketch, "E1052", {"start": v(1491.63, 857.7) * mm, "end": v(1491.63, 848.4) * mm});
            skLineSegment(sketch, "E1053", {"start": v(1491.63, 848.4) * mm, "end": v(1439.95, 838.22) * mm});
            skLineSegment(sketch, "E1054", {"start": v(1439.95, 838.22) * mm, "end": v(1439.95, 869.2) * mm});
            skLineSegment(sketch, "E1055", {"start": v(1440.46, 1090.23) * mm, "end": v(1491.58, 1078.84) * mm});
            skLineSegment(sketch, "E1056", {"start": v(1491.58, 1078.84) * mm, "end": v(1491.58, 1069.52) * mm});
            skLineSegment(sketch, "E1057", {"start": v(1491.58, 1069.52) * mm, "end": v(1440.46, 1059.57) * mm});
            skLineSegment(sketch, "E1058", {"start": v(1440.46, 1059.57) * mm, "end": v(1440.46, 1090.23) * mm});
            skLineSegment(sketch, "E1059", {"start": v(1440.25, 651.84) * mm, "end": v(1440.25, 621.12) * mm});
            skLineSegment(sketch, "E1060", {"start": v(1800.32, 15.94) * mm, "end": v(1851.74, 4.79) * mm});
            skLineSegment(sketch, "E1061", {"start": v(1851.74, 4.79) * mm, "end": v(1851.74, -4.95) * mm});
            skLineSegment(sketch, "E1062", {"start": v(1851.74, -4.95) * mm, "end": v(1800.32, -14.69) * mm});
            skLineSegment(sketch, "E1063", {"start": v(1800.32, -14.69) * mm, "end": v(1800.32, 15.94) * mm});
            skLineSegment(sketch, "E1064", {"start": v(1800.22, -398.33) * mm, "end": v(1800.22, -428.69) * mm});
            skLineSegment(sketch, "E1065", {"start": v(1800.22, -398.33) * mm, "end": v(1851.56, -409.64) * mm});
            skLineSegment(sketch, "E1066", {"start": v(1851.56, -409.64) * mm, "end": v(1851.56, -418.87) * mm});
            skLineSegment(sketch, "E1067", {"start": v(1851.56, -418.87) * mm, "end": v(1800.22, -428.69) * mm});
            skLineSegment(sketch, "E1068", {"start": v(1800.4, -187.6) * mm, "end": v(1851.51, -198.77) * mm});
            skLineSegment(sketch, "E1069", {"start": v(1851.51, -198.77) * mm, "end": v(1851.51, -208.37) * mm});
            skLineSegment(sketch, "E1070", {"start": v(1851.51, -208.37) * mm, "end": v(1800.32, -218.19) * mm});
            skLineSegment(sketch, "E1071", {"start": v(1800.32, -218.19) * mm, "end": v(1800.4, -187.6) * mm});
            skLineSegment(sketch, "E1072", {"start": v(1800.35, 221.55) * mm, "end": v(1851.62, 210.24) * mm});
            skLineSegment(sketch, "E1073", {"start": v(1851.62, 210.24) * mm, "end": v(1851.62, 200.64) * mm});
            skLineSegment(sketch, "E1074", {"start": v(1851.62, 200.64) * mm, "end": v(1800.28, 190.82) * mm});
            skLineSegment(sketch, "E1075", {"start": v(1800.28, 190.82) * mm, "end": v(1800.35, 221.55) * mm});
            skLineSegment(sketch, "E1076", {"start": v(1800.5, 429.32) * mm, "end": v(1851.47, 417.73) * mm});
            skLineSegment(sketch, "E1077", {"start": v(1851.47, 417.73) * mm, "end": v(1851.47, 408.44) * mm});
            skLineSegment(sketch, "E1078", {"start": v(1851.47, 408.44) * mm, "end": v(1800.5, 398.7) * mm});
            skLineSegment(sketch, "E1079", {"start": v(1800.5, 398.7) * mm, "end": v(1800.5, 429.32) * mm});
            skLineSegment(sketch, "E1080", {"start": v(1800.3, 651.84) * mm, "end": v(1851.57, 640.31) * mm});
            skLineSegment(sketch, "E1081", {"start": v(1851.57, 640.31) * mm, "end": v(1851.57, 631.09) * mm});
            skLineSegment(sketch, "E1082", {"start": v(1851.57, 631.09) * mm, "end": v(1800.3, 621.12) * mm});
            skLineSegment(sketch, "E1083", {"start": v(1800.02, 869.2) * mm, "end": v(1851.69, 857.7) * mm});
            skLineSegment(sketch, "E1084", {"start": v(1851.69, 857.7) * mm, "end": v(1851.69, 848.4) * mm});
            skLineSegment(sketch, "E1085", {"start": v(1851.69, 848.4) * mm, "end": v(1800.02, 838.22) * mm});
            skLineSegment(sketch, "E1086", {"start": v(1800.02, 838.22) * mm, "end": v(1800.02, 869.2) * mm});
            skLineSegment(sketch, "E1087", {"start": v(1800.52, 1090.23) * mm, "end": v(1851.64, 1078.84) * mm});
            skLineSegment(sketch, "E1088", {"start": v(1851.64, 1078.84) * mm, "end": v(1851.64, 1069.52) * mm});
            skLineSegment(sketch, "E1089", {"start": v(1851.64, 1069.52) * mm, "end": v(1800.52, 1059.57) * mm});
            skLineSegment(sketch, "E1090", {"start": v(1800.52, 1059.57) * mm, "end": v(1800.52, 1090.23) * mm});
            skLineSegment(sketch, "E1091", {"start": v(1800.3, 651.84) * mm, "end": v(1800.3, 621.12) * mm});
            skLineSegment(sketch, "E1092", {"start": v(2186.2, 15.69) * mm, "end": v(2237.61, 4.53) * mm});
            skLineSegment(sketch, "E1093", {"start": v(2237.61, 4.53) * mm, "end": v(2237.61, -5.2) * mm});
            skLineSegment(sketch, "E1094", {"start": v(2237.61, -5.2) * mm, "end": v(2186.2, -14.94) * mm});
            skLineSegment(sketch, "E1095", {"start": v(2186.2, -14.94) * mm, "end": v(2186.2, 15.69) * mm});
            skLineSegment(sketch, "E1096", {"start": v(2186.1, -398.58) * mm, "end": v(2186.1, -428.94) * mm});
            skLineSegment(sketch, "E1097", {"start": v(2186.1, -398.58) * mm, "end": v(2237.44, -409.9) * mm});
            skLineSegment(sketch, "E1098", {"start": v(2237.44, -409.9) * mm, "end": v(2237.44, -419.12) * mm});
            skLineSegment(sketch, "E1099", {"start": v(2237.44, -419.12) * mm, "end": v(2186.1, -428.94) * mm});
            skLineSegment(sketch, "E1100", {"start": v(2186.27, -187.86) * mm, "end": v(2237.39, -199.02) * mm});
            skLineSegment(sketch, "E1101", {"start": v(2237.39, -199.02) * mm, "end": v(2237.39, -208.62) * mm});
            skLineSegment(sketch, "E1102", {"start": v(2237.39, -208.62) * mm, "end": v(2186.2, -218.44) * mm});
            skLineSegment(sketch, "E1103", {"start": v(2186.2, -218.44) * mm, "end": v(2186.27, -187.86) * mm});
            skLineSegment(sketch, "E1104", {"start": v(2186.23, 221.3) * mm, "end": v(2237.5, 209.99) * mm});
            skLineSegment(sketch, "E1105", {"start": v(2237.5, 209.99) * mm, "end": v(2237.5, 200.39) * mm});
            skLineSegment(sketch, "E1106", {"start": v(2237.5, 200.39) * mm, "end": v(2186.16, 190.57) * mm});
            skLineSegment(sketch, "E1107", {"start": v(2186.16, 190.57) * mm, "end": v(2186.23, 221.3) * mm});
            skLineSegment(sketch, "E1108", {"start": v(2186.39, 429.07) * mm, "end": v(2237.35, 417.48) * mm});
            skLineSegment(sketch, "E1109", {"start": v(2237.35, 417.48) * mm, "end": v(2237.35, 408.2) * mm});
            skLineSegment(sketch, "E1110", {"start": v(2237.35, 408.2) * mm, "end": v(2186.39, 398.46) * mm});
            skLineSegment(sketch, "E1111", {"start": v(2186.39, 398.46) * mm, "end": v(2186.39, 429.07) * mm});
            skLineSegment(sketch, "E1112", {"start": v(2186.19, 651.6) * mm, "end": v(2237.45, 640.06) * mm});
            skLineSegment(sketch, "E1113", {"start": v(2237.45, 640.06) * mm, "end": v(2237.45, 630.83) * mm});
            skLineSegment(sketch, "E1114", {"start": v(2237.45, 630.83) * mm, "end": v(2186.19, 620.86) * mm});
            skLineSegment(sketch, "E1115", {"start": v(2185.9, 868.94) * mm, "end": v(2237.57, 857.44) * mm});
            skLineSegment(sketch, "E1116", {"start": v(2237.57, 857.44) * mm, "end": v(2237.57, 848.15) * mm});
            skLineSegment(sketch, "E1117", {"start": v(2237.57, 848.15) * mm, "end": v(2185.9, 837.97) * mm});
            skLineSegment(sketch, "E1118", {"start": v(2185.9, 837.97) * mm, "end": v(2185.9, 868.94) * mm});
            skLineSegment(sketch, "E1119", {"start": v(2186.4, 1089.98) * mm, "end": v(2237.52, 1078.6) * mm});
            skLineSegment(sketch, "E1120", {"start": v(2237.52, 1078.6) * mm, "end": v(2237.52, 1069.27) * mm});
            skLineSegment(sketch, "E1121", {"start": v(2237.52, 1069.27) * mm, "end": v(2186.4, 1059.32) * mm});
            skLineSegment(sketch, "E1122", {"start": v(2186.4, 1059.32) * mm, "end": v(2186.4, 1089.98) * mm});
            skLineSegment(sketch, "E1123", {"start": v(2186.19, 651.6) * mm, "end": v(2186.19, 620.86) * mm});
            skLineSegment(sketch, "E1124", {"start": v(2546.26, 15.69) * mm, "end": v(2597.68, 4.53) * mm});
            skLineSegment(sketch, "E1125", {"start": v(2597.68, 4.53) * mm, "end": v(2597.68, -5.2) * mm});
            skLineSegment(sketch, "E1126", {"start": v(2597.68, -5.2) * mm, "end": v(2546.26, -14.94) * mm});
            skLineSegment(sketch, "E1127", {"start": v(2546.26, -14.94) * mm, "end": v(2546.26, 15.69) * mm});
            skLineSegment(sketch, "E1128", {"start": v(2546.16, -398.58) * mm, "end": v(2546.16, -428.94) * mm});
            skLineSegment(sketch, "E1129", {"start": v(2546.16, -398.58) * mm, "end": v(2597.5, -409.9) * mm});
            skLineSegment(sketch, "E1130", {"start": v(2597.5, -409.9) * mm, "end": v(2597.5, -419.12) * mm});
            skLineSegment(sketch, "E1131", {"start": v(2597.5, -419.12) * mm, "end": v(2546.16, -428.94) * mm});
            skLineSegment(sketch, "E1132", {"start": v(2546.34, -187.86) * mm, "end": v(2597.45, -199.02) * mm});
            skLineSegment(sketch, "E1133", {"start": v(2597.45, -199.02) * mm, "end": v(2597.45, -208.62) * mm});
            skLineSegment(sketch, "E1134", {"start": v(2597.45, -208.62) * mm, "end": v(2546.26, -218.44) * mm});
            skLineSegment(sketch, "E1135", {"start": v(2546.26, -218.44) * mm, "end": v(2546.34, -187.86) * mm});
            skLineSegment(sketch, "E1136", {"start": v(2546.3, 221.3) * mm, "end": v(2597.56, 209.99) * mm});
            skLineSegment(sketch, "E1137", {"start": v(2597.56, 209.99) * mm, "end": v(2597.56, 200.39) * mm});
            skLineSegment(sketch, "E1138", {"start": v(2597.56, 200.39) * mm, "end": v(2546.22, 190.57) * mm});
            skLineSegment(sketch, "E1139", {"start": v(2546.22, 190.57) * mm, "end": v(2546.3, 221.3) * mm});
            skLineSegment(sketch, "E1140", {"start": v(2546.45, 429.07) * mm, "end": v(2597.41, 417.48) * mm});
            skLineSegment(sketch, "E1141", {"start": v(2597.41, 417.48) * mm, "end": v(2597.41, 408.2) * mm});
            skLineSegment(sketch, "E1142", {"start": v(2597.41, 408.2) * mm, "end": v(2546.45, 398.46) * mm});
            skLineSegment(sketch, "E1143", {"start": v(2546.45, 398.46) * mm, "end": v(2546.45, 429.07) * mm});
            skLineSegment(sketch, "E1144", {"start": v(2546.25, 651.6) * mm, "end": v(2597.51, 640.06) * mm});
            skLineSegment(sketch, "E1145", {"start": v(2597.51, 640.06) * mm, "end": v(2597.51, 630.83) * mm});
            skLineSegment(sketch, "E1146", {"start": v(2597.51, 630.83) * mm, "end": v(2546.25, 620.86) * mm});
            skLineSegment(sketch, "E1147", {"start": v(2545.96, 868.94) * mm, "end": v(2597.63, 857.44) * mm});
            skLineSegment(sketch, "E1148", {"start": v(2597.63, 857.44) * mm, "end": v(2597.63, 848.15) * mm});
            skLineSegment(sketch, "E1149", {"start": v(2597.63, 848.15) * mm, "end": v(2545.96, 837.97) * mm});
            skLineSegment(sketch, "E1150", {"start": v(2545.96, 837.97) * mm, "end": v(2545.96, 868.94) * mm});
            skLineSegment(sketch, "E1151", {"start": v(2546.46, 1089.98) * mm, "end": v(2597.58, 1078.6) * mm});
            skLineSegment(sketch, "E1152", {"start": v(2597.58, 1078.6) * mm, "end": v(2597.58, 1069.27) * mm});
            skLineSegment(sketch, "E1153", {"start": v(2597.58, 1069.27) * mm, "end": v(2546.46, 1059.32) * mm});
            skLineSegment(sketch, "E1154", {"start": v(2546.46, 1059.32) * mm, "end": v(2546.46, 1089.98) * mm});
            skLineSegment(sketch, "E1155", {"start": v(2546.25, 651.6) * mm, "end": v(2546.25, 620.86) * mm});
            skSolve(sketch);
        }
        {
            var Q0;
            Q0=qSketchRegion(id+"F6",true);
            extrude(context, id + "F7", {"entities" : qUnion([Q0]), "depth" : 7.62 * mm, "offsetDistance" : 25.4 * mm});
        }
    });
